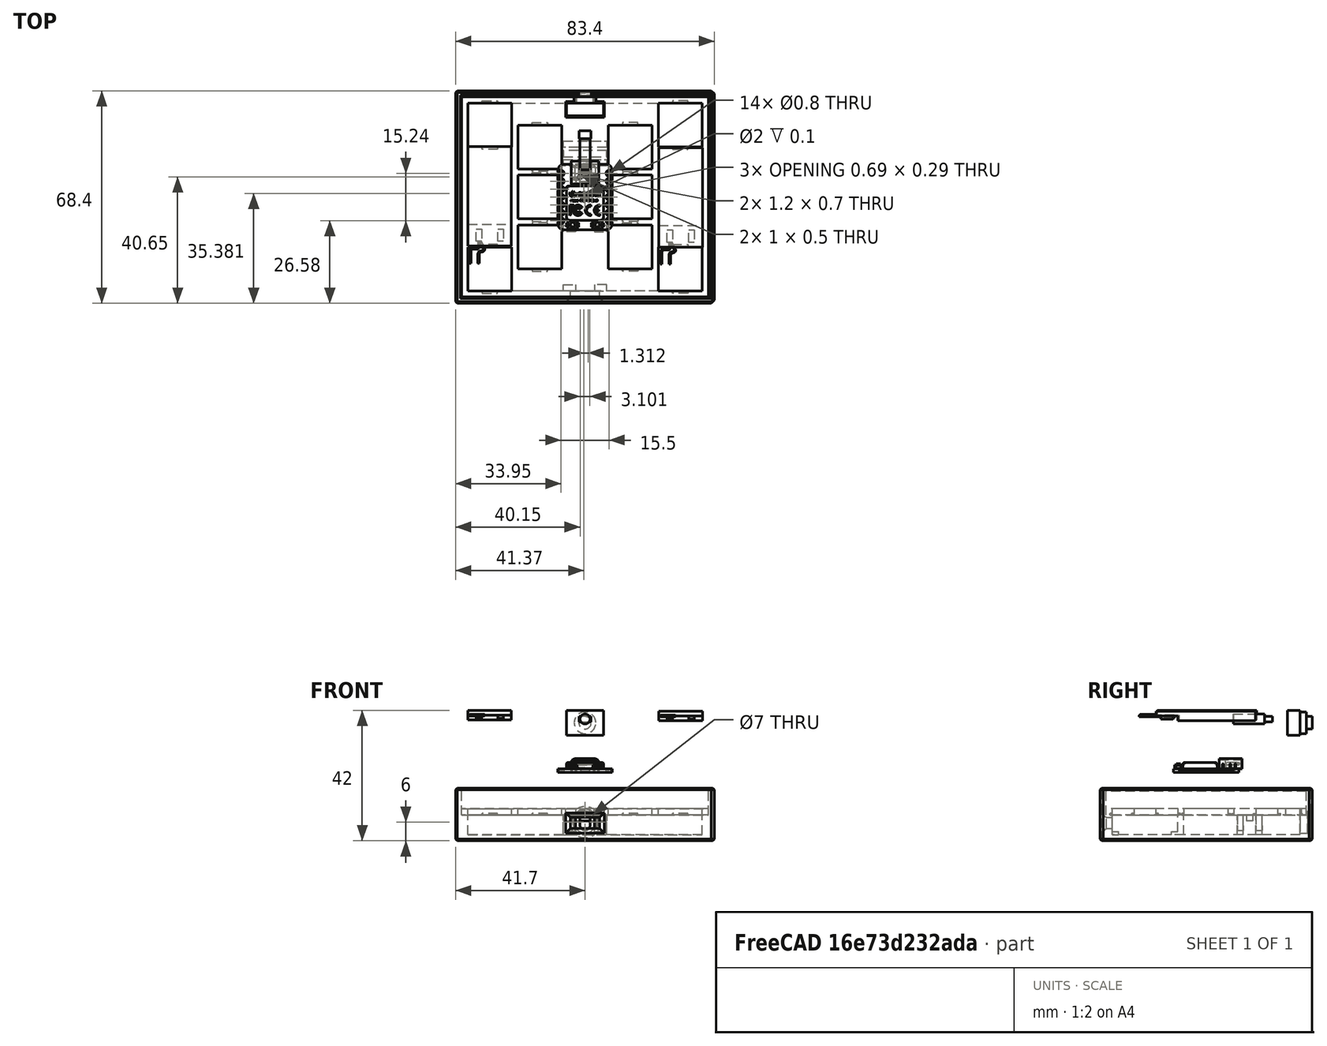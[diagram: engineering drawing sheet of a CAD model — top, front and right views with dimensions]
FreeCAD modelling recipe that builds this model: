
FCSTD DOCUMENT  (FreeCAD 0.20R)
Label: braille_keyboard
License: All rights reserved
LicenseURL: http://en.wikipedia.org/wiki/All_rights_reserved
objects: Sketcher::SketchObject×29, PartDesign::Pad×18, Mesh::Feature×10, Part::Feature×10, PartDesign::Body×6, App::Part×4, PartDesign::Plane×4, PartDesign::AdditivePipe×4, PartDesign::Pocket×3, Part::Chamfer×2, Spreadsheet::Sheet×1, Part::Box×1, Part::Cylinder×1, Part::MultiFuse×1, Part::Cut×1, PartDesign::Mirrored×1
note: 106 computed .brp shape members not serialized (recipe doc carries the construction recipe); baked Part::Feature solids carry a one-line shape summary decoded from their .brp

FEATURE [Spreadsheet::Sheet] Spreadsheet
  cells = A1=chamfer; B1=key size; C1=spacing; D1=walls; F1=xiauo width; G1=xiao length; H1=xiao height; I1=usb width; J1=usb height; A2(chamfer)==2mm; B2(keysize)==14.1mm; C2(spacing)==2mm; D2(walls)==2mm; F2(xiao_width)==18mm; G2(xiao_length)==21mm; I2(usb_width)==9.5mm; J2(usb_height)==3.5mm; C3=outer space; A4=mx height below; B4=mx height above; C4(outer_space)==2mm; F4=xiao add distance; A5(mx_height_below)==3.3mm + 5mm; B5(mx_height_above)==6.6mm; F5(xiao_add_dist)==-5mm; A8=pwr switch dia; B8=pwr switch height; A9(switch_dia)==7mm; B9(switch_height)==8mm; B13=Positioning of MX switches; B15=col1; C15=col2; D15=col3; E15=col4; B16(col1)==col2 - (keysize + spacing); C16(col2)==-((xiao_width + xiao_add_dist) / 2 + (keysize + spacing) / 2); D16(col3)==(xiao_width + xiao_add_dist) / 2 + (keysize + spacing) / 2; E16(col4)==col3 + keysize + spacing; B18=row1; C18=row2; D18=row3; E18=row4; B19(row1)==row2 + keysize + spacing; C19(row2)==0mm; D19(row3)==-(row2 + keysize + spacing); E19(row4)==row3 - keysize / 2; B22=snaplength; C22=snapwidth; B23(snaplength)==spacing / 2 - spacing / 10; C23(snapwidth)==5mm
FEATURE [Sketcher::SketchObject] Sketch001
  AttachmentOffset = pos=(0,0,20) rot=(0,0,1;0rad)
  FullyConstrained = true
  MapMode = 5
  Placement = pos=(0,0,20) rot=(0,0,1;0rad)
  Support = -> [XY_Plane001]
  expr: Constraints[8] = <<Spreadsheet>>.keysize * 4 + <<Spreadsheet>>.spacing * 2 + <<Spreadsheet>>.outer_space * 2 + <<Spreadsheet>>.walls * 2
  expr: Constraints[9] = <<Spreadsheet>>.keysize * 4 + <<Spreadsheet>>.spacing * 3 + <<Spreadsheet>>.outer_space * 2 + <<Spreadsheet>>.walls * 2 + <<Spreadsheet>>.xiao_width + <<Spreadsheet>>.xiao_add_dist
  sketch-geometry (8):
    g0: LineSegment StartX=-41.7 StartY=34.2 StartZ=0 EndX=41.7 EndY=34.2 EndZ=0
    g1: LineSegment StartX=41.7 StartY=34.2 StartZ=0 EndX=41.7 EndY=-34.2 EndZ=0
    g2: LineSegment StartX=41.7 StartY=-34.2 StartZ=0 EndX=-41.7 EndY=-34.2 EndZ=0
    g3: LineSegment StartX=-41.7 StartY=-34.2 StartZ=0 EndX=-41.7 EndY=34.2 EndZ=0
    g4: LineSegment StartX=-41.7 StartY=34.2 StartZ=0 EndX=41.7 EndY=34.2 EndZ=0
    g5: LineSegment StartX=41.7 StartY=34.2 StartZ=0 EndX=41.7 EndY=-34.2 EndZ=0
    g6: LineSegment StartX=41.7 StartY=-34.2 StartZ=0 EndX=-41.7 EndY=-34.2 EndZ=0
    g7: LineSegment StartX=-41.7 StartY=-34.2 StartZ=0 EndX=-41.7 EndY=34.2 EndZ=0
  constraints (20):
    c: Coincident(g0,g1)
    c: Coincident(g1,g2)
    c: Coincident(g2,g3)
    c: Coincident(g3,g0)
    c: Horizontal(g2)
    c: Vertical(g1)
    c: Symmetric(g0,g0,g-2)
    c: Symmetric(g2,g0,g-1)
    c: DistanceY(g3,g3) = 68.4
    c: DistanceX(g0,g0) = 83.4
    c: Coincident(g4,g5)
    c: Coincident(g5,g6)
    c: Coincident(g6,g7)
    c: Coincident(g7,g4)
    c: Horizontal(g4)
    c: Horizontal(g6)
    c: Vertical(g5)
    c: Vertical(g7)
    c: Coincident(g4,g0)
    c: Coincident(g5,g1)
FEATURE [PartDesign::Pad] Pad001  label="Bottom"
  Direction = (0,0,1)
  Length = 2
  Length2 = 10
  Profile = -> Sketch001
  ReferenceAxis = -> Sketch001 [N_Axis]
  Type = 0
  expr: Length = <<Spreadsheet>>.walls
FEATURE [Sketcher::SketchObject] Sketch002
  ExternalGeometry = -> [Pad001]
  FullyConstrained = true
  MapMode = 5
  Placement = pos=(0,0,20) rot=(1,0,0;3.14159rad)
  Support = -> [Pad001]
  expr: Constraints[16] = <<Spreadsheet>>.walls + <<Spreadsheet>>.outer_space
  expr: Constraints[19] = <<Spreadsheet>>.walls + <<Spreadsheet>>.outer_space
  sketch-geometry (8):
    g0: LineSegment StartX=-41.7 StartY=34.2 StartZ=0 EndX=41.7 EndY=34.2 EndZ=0
    g1: LineSegment StartX=41.7 StartY=34.2 StartZ=0 EndX=41.7 EndY=-34.2 EndZ=0
    g2: LineSegment StartX=41.7 StartY=-34.2 StartZ=0 EndX=-41.7 EndY=-34.2 EndZ=0
    g3: LineSegment StartX=-41.7 StartY=-34.2 StartZ=0 EndX=-41.7 EndY=34.2 EndZ=0
    g4: LineSegment StartX=-37.7 StartY=30.2 StartZ=0 EndX=37.7 EndY=30.2 EndZ=0
    g5: LineSegment StartX=37.7 StartY=30.2 StartZ=0 EndX=37.7 EndY=-30.2 EndZ=0
    g6: LineSegment StartX=37.7 StartY=-30.2 StartZ=0 EndX=-37.7 EndY=-30.2 EndZ=0
    g7: LineSegment StartX=-37.7 StartY=-30.2 StartZ=0 EndX=-37.7 EndY=30.2 EndZ=0
  constraints (20):
    c: Coincident(g0,g1)
    c: Coincident(g1,g2)
    c: Coincident(g2,g3)
    c: Coincident(g3,g0)
    c: Horizontal(g0)
    c: Horizontal(g2)
    c: Vertical(g1)
    c: Vertical(g3)
    c: Coincident(g0,g-4)
    c: Coincident(g1,g-6)
    c: Coincident(g4,g5)
    c: Coincident(g5,g6)
    c: Coincident(g6,g7)
    c: Coincident(g7,g4)
    c: Horizontal(g6)
    c: Vertical(g5)
    c: DistanceX(g0,g4) = 4
    c: Symmetric(g4,g4,g-2)
    c: Symmetric(g4,g6,g-1)
    c: DistanceY(g4,g0) = 4
FEATURE [PartDesign::Pad] Pad002  label="PlateRest"
  BaseFeature = -> Pad001
  Direction = (0,0,-1)
  Length = 6.3
  Length2 = 10
  Profile = -> Sketch002
  ReferenceAxis = -> Sketch002 [N_Axis]
  Type = 0
  expr: Length = <<Spreadsheet>>.mx_height_below - <<Spreadsheet>>.walls
FEATURE [Sketcher::SketchObject] Sketch003
  ExternalGeometry = -> [Pad002]
  FullyConstrained = true
  MapMode = 5
  Placement = pos=(0,0,13.7) rot=(1,0,0;3.14159rad)
  Support = -> [Pad002]
  expr: Constraints[8] = <<Spreadsheet>>.walls
  expr: Constraints[9] = <<Spreadsheet>>.walls
  sketch-geometry (8):
    g0: LineSegment StartX=-39.7 StartY=32.2 StartZ=0 EndX=39.7 EndY=32.2 EndZ=0
    g1: LineSegment StartX=39.7 StartY=32.2 StartZ=0 EndX=39.7 EndY=-32.2 EndZ=0
    g2: LineSegment StartX=39.7 StartY=-32.2 StartZ=0 EndX=-39.7 EndY=-32.2 EndZ=0
    g3: LineSegment StartX=-39.7 StartY=-32.2 StartZ=0 EndX=-39.7 EndY=32.2 EndZ=0
    g4: LineSegment StartX=-41.7 StartY=34.2 StartZ=0 EndX=41.7 EndY=34.2 EndZ=0
    g5: LineSegment StartX=41.7 StartY=34.2 StartZ=0 EndX=41.7 EndY=-34.2 EndZ=0
    g6: LineSegment StartX=41.7 StartY=-34.2 StartZ=0 EndX=-41.7 EndY=-34.2 EndZ=0
    g7: LineSegment StartX=-41.7 StartY=-34.2 StartZ=0 EndX=-41.7 EndY=34.2 EndZ=0
  constraints (20):
    c: Coincident(g0,g1)
    c: Coincident(g1,g2)
    c: Coincident(g2,g3)
    c: Coincident(g3,g0)
    c: Horizontal(g2)
    c: Vertical(g1)
    c: Symmetric(g0,g0,g-2)
    c: Symmetric(g2,g0,g-1)
    c: DistanceY(g0,g-5) = 2
    c: DistanceX(g-5,g0) = 2
    c: Coincident(g4,g5)
    c: Coincident(g5,g6)
    c: Coincident(g6,g7)
    c: Coincident(g7,g4)
    c: Horizontal(g4)
    c: Horizontal(g6)
    c: Vertical(g5)
    c: Vertical(g7)
    c: Coincident(g4,g-5)
    c: Coincident(g5,g-6)
FEATURE [PartDesign::Pad] Pad003  label="OuterWall"
  BaseFeature = -> Pad002
  Direction = (0,0,-1)
  Length = 8.6
  Length2 = 10
  Profile = -> Sketch003
  ReferenceAxis = -> Sketch003 [N_Axis]
  Type = 0
  expr: Length = <<Spreadsheet>>.mx_height_above + <<Spreadsheet>>.walls
FEATURE [Mesh::Feature] switch_mx
  Placement = pos=(14.55,16.1,-1.4) rot=(1,0,0;3.14159rad)
  expr: .Placement.Base.x = <<Spreadsheet>>.col3
  expr: .Placement.Base.y = <<Spreadsheet>>.row1
FEATURE [Mesh::Feature] switch_mx001
  Placement = pos=(-14.55,0,-1.4) rot=(1,0,0;3.14159rad)
  expr: .Placement.Base.x = <<Spreadsheet>>.col2
  expr: .Placement.Base.y = <<Spreadsheet>>.row2
FEATURE [Sketcher::SketchObject] Sketch004
  ExternalGeometry = -> [Pad003]
  FullyConstrained = true
  MapMode = 5
  Placement = pos=(0,0,20) rot=(1,0,0;3.14159rad)
  Support = -> [Pad003]
  expr: Constraints[13] = <<Spreadsheet>>.walls
  expr: Constraints[28] = <<Spreadsheet>>.walls
  expr: Constraints[39] = <<Spreadsheet>>.walls
  expr: Constraints[40] = <<Spreadsheet>>.walls * 2
  expr: Constraints[60] = <<Spreadsheet>>.walls
  expr: Constraints[63] = 2 * <<Spreadsheet>>.walls
  expr: Constraints[7] = <<Spreadsheet>>.xiao_width
  expr: Constraints[8] = <<Spreadsheet>>.xiao_length
  sketch-geometry (22):
    g0: LineSegment StartX=-9 StartY=30.2 StartZ=0 EndX=9 EndY=30.2 EndZ=0
    g1: LineSegment StartX=9 StartY=30.2 StartZ=0 EndX=9 EndY=9.2 EndZ=0
    g2: LineSegment StartX=9 StartY=9.2 StartZ=0 EndX=-9 EndY=9.2 EndZ=0
    g3: LineSegment StartX=-9 StartY=9.2 StartZ=0 EndX=-9 EndY=30.2 EndZ=0
    g4: LineSegment StartX=-7 StartY=9.2 StartZ=0 EndX=-7 EndY=-30.2 EndZ=0
    g5: LineSegment StartX=7 StartY=9.2 StartZ=0 EndX=7 EndY=-30.2 EndZ=0
    g6: LineSegment StartX=-7 StartY=-10 StartZ=0 EndX=7 EndY=-10 EndZ=0
    g7: LineSegment StartX=7 StartY=-10 StartZ=0 EndX=7 EndY=-12 EndZ=0
    g8: LineSegment StartX=7 StartY=-12 StartZ=0 EndX=-7 EndY=-12 EndZ=0
    g9: LineSegment StartX=-7 StartY=-12 StartZ=0 EndX=-7 EndY=-10 EndZ=0
    g10: LineSegment StartX=-7 StartY=-16 StartZ=0 EndX=7 EndY=-16 EndZ=0
    g11: LineSegment StartX=7 StartY=-16 StartZ=0 EndX=7 EndY=-18 EndZ=0
    g12: LineSegment StartX=7 StartY=-18 StartZ=0 EndX=-7 EndY=-18 EndZ=0
    g13: LineSegment StartX=-7 StartY=-18 StartZ=0 EndX=-7 EndY=-16 EndZ=0
    g14: LineSegment StartX=-7 StartY=9.2 StartZ=0 EndX=-3 EndY=9.2 EndZ=0
    g15: LineSegment StartX=-3 StartY=9.2 StartZ=0 EndX=-3 EndY=7.2 EndZ=0
    g16: LineSegment StartX=-3 StartY=7.2 StartZ=0 EndX=-7 EndY=7.2 EndZ=0
    g17: LineSegment StartX=-7 StartY=7.2 StartZ=0 EndX=-7 EndY=9.2 EndZ=0
    g18: LineSegment StartX=3 StartY=9.2 StartZ=0 EndX=7 EndY=9.2 EndZ=0
    g19: LineSegment StartX=7 StartY=9.2 StartZ=0 EndX=7 EndY=7.2 EndZ=0
    g20: LineSegment StartX=7 StartY=7.2 StartZ=0 EndX=3 EndY=7.2 EndZ=0
    g21: LineSegment StartX=3 StartY=7.2 StartZ=0 EndX=3 EndY=9.2 EndZ=0
  constraints (64):
    c: Coincident(g0,g1)
    c: Coincident(g1,g2)
    c: Coincident(g2,g3)
    c: Coincident(g3,g0)
    c: Horizontal(g2)
    c: Vertical(g1)
    c: Vertical(g3)
    c: DistanceX(g0,g0) = 18
    c: DistanceY(g1,g1) = 21
    c: Symmetric(g0,g0,g-2)
    c: PointOnObject(g0,g-3)
    c: PointOnObject(g4,g2)
    c: Symmetric(g4,g5,g-2)
    c: DistanceX(g2,g4) = 2
    c: PointOnObject(g4,g-6)
    c: Vertical(g4)
    c: PointOnObject(g5,g-6)
    c: Vertical(g5)
    c: Coincident(g6,g7)
    c: Coincident(g7,g8)
    c: Coincident(g8,g9)
    c: Coincident(g9,g6)
    c: Horizontal(g6)
    c: Horizontal(g8)
    c: Vertical(g7)
    c: Vertical(g9)
    c: PointOnObject(g6,g4)
    c: PointOnObject(g7,g5)
    c: DistanceY(g7,g7) = 2
    c: Coincident(g10,g11)
    c: Coincident(g11,g12)
    c: Coincident(g12,g13)
    c: Coincident(g13,g10)
    c: Horizontal(g10)
    c: Horizontal(g12)
    c: Vertical(g11)
    c: Vertical(g13)
    c: PointOnObject(g10,g4)
    c: PointOnObject(g11,g5)
    c: DistanceY(g11,g11) = 2
    c: DistanceY(g10,g7) = 4
    c: DistanceY(g6,g-1) = 10
    c: Coincident(g14,g15)
    c: Coincident(g15,g16)
    c: Coincident(g16,g17)
    c: Coincident(g17,g14)
    c: Horizontal(g14)
    c: Horizontal(g16)
    c: Vertical(g15)
    c: Vertical(g17)
    c: Coincident(g14,g4)
    c: Coincident(g18,g19)
    c: Coincident(g19,g20)
    c: Coincident(g20,g21)
    c: Coincident(g21,g18)
    c: Horizontal(g18)
    c: Horizontal(g20)
    c: Vertical(g19)
    c: Vertical(g21)
    c: PointOnObject(g19,g5)
    c: DistanceY(g15,g15) = 2
    c: Equal(g15,g21)
    c: Symmetric(g18,g14,g-2)
    c: DistanceX(g20,g20) = 4
FEATURE [PartDesign::Pad] Pad004  label="xiaoholder"
  BaseFeature = -> Pad003
  Direction = (0,0,-1)
  Length = 6.3
  Length2 = 10
  Profile = -> Sketch004
  ReferenceAxis = -> Sketch004 [N_Axis]
  Type = 0
  expr: Length = <<Spreadsheet>>.mx_height_below - <<Spreadsheet>>.walls
FEATURE [Sketcher::SketchObject] Sketch005
  ExternalGeometry = -> [Pad004]
  FullyConstrained = true
  MapMode = 5
  Placement = pos=(0,0,20) rot=(1,0,0;3.14159rad)
  Support = -> [Pad004]
  expr: Constraints[25] = <<Spreadsheet>>.walls
  expr: Constraints[9] = <<Spreadsheet>>.walls
  sketch-geometry (20):
    g0: LineSegment StartX=-7 StartY=9.2 StartZ=0 EndX=-3 EndY=9.2 EndZ=0
    g1: LineSegment StartX=-3 StartY=9.2 StartZ=0 EndX=-3 EndY=11.2 EndZ=0
    g2: LineSegment StartX=-3 StartY=11.2 StartZ=0 EndX=-7 EndY=11.2 EndZ=0
    g3: LineSegment StartX=-7 StartY=11.2 StartZ=0 EndX=-7 EndY=9.2 EndZ=0
    g4: LineSegment StartX=-3 StartY=30.2 StartZ=0 EndX=-7 EndY=30.2 EndZ=0
    g5: LineSegment StartX=-7 StartY=30.2 StartZ=0 EndX=-7 EndY=28.2 EndZ=0
    g6: LineSegment StartX=-7 StartY=28.2 StartZ=0 EndX=-3 EndY=28.2 EndZ=0
    g7: LineSegment StartX=-3 StartY=28.2 StartZ=0 EndX=-3 EndY=30.2 EndZ=0
    g8: LineSegment StartX=-3 StartY=11.2 StartZ=0 EndX=-3 EndY=30.2 EndZ=0
    g9: LineSegment StartX=-7 StartY=11.2 StartZ=0 EndX=-7 EndY=30.2 EndZ=0
    g10: LineSegment StartX=7 StartY=9.2 StartZ=0 EndX=3 EndY=9.2 EndZ=0
    g11: LineSegment StartX=3 StartY=9.2 StartZ=0 EndX=3 EndY=11.2 EndZ=0
    g12: LineSegment StartX=3 StartY=11.2 StartZ=0 EndX=7 EndY=11.2 EndZ=0
    g13: LineSegment StartX=7 StartY=11.2 StartZ=0 EndX=7 EndY=9.2 EndZ=0
    g14: LineSegment StartX=3 StartY=30.2 StartZ=0 EndX=7 EndY=30.2 EndZ=0
    g15: LineSegment StartX=7 StartY=30.2 StartZ=0 EndX=7 EndY=28.2 EndZ=0
    g16: LineSegment StartX=7 StartY=28.2 StartZ=0 EndX=3 EndY=28.2 EndZ=0
    g17: LineSegment StartX=3 StartY=28.2 StartZ=0 EndX=3 EndY=30.2 EndZ=0
    g18: LineSegment StartX=3 StartY=11.2 StartZ=0 EndX=3 EndY=30.2 EndZ=0
    g19: LineSegment StartX=7 StartY=11.2 StartZ=0 EndX=7 EndY=30.2 EndZ=0
  constraints (52):
    c: Coincident(g0,g1)
    c: Coincident(g1,g2)
    c: Coincident(g2,g3)
    c: Coincident(g3,g0)
    c: Horizontal(g2)
    c: Vertical(g1)
    c: Vertical(g3)
    c: Coincident(g0,g-3)
    c: Coincident(g0,g-3)
    c: DistanceY(g1,g1) = 2
    c: Coincident(g4,g5)
    c: Coincident(g5,g6)
    c: Coincident(g6,g7)
    c: Coincident(g7,g4)
    c: Horizontal(g4)
    c: Horizontal(g6)
    c: Vertical(g5)
    c: Vertical(g7)
    c: PointOnObject(g4,g-4)
    c: Coincident(g8,g1)
    c: Vertical(g8)
    c: Coincident(g9,g2)
    c: Vertical(g9)
    c: Coincident(g4,g9)
    c: Coincident(g4,g8)
    c: DistanceY(g5,g5) = 2
    c: Coincident(g10,g11)
    c: Coincident(g11,g12)
    c: Coincident(g12,g13)
    c: Coincident(g13,g10)
    c: Horizontal(g12)
    c: Vertical(g11)
    c: Vertical(g13)
    c: Coincident(g14,g15)
    c: Coincident(g15,g16)
    c: Coincident(g16,g17)
    c: Coincident(g17,g14)
    c: Horizontal(g14)
    c: Horizontal(g16)
    c: Vertical(g15)
    c: Vertical(g17)
    c: Coincident(g18,g11)
    c: Coincident(g19,g12)
    c: Vertical(g19)
    c: Coincident(g14,g19)
    c: Coincident(g14,g18)
    c: Symmetric(g14,g4,g-2)
    c: Equal(g17,g7)
    c: Symmetric(g11,g1,g-2)
    c: Equal(g11,g1)
    c: Horizontal(g10)
    c: Equal(g12,g2)
FEATURE [PartDesign::Pad] Pad005  label="xiaorest"
  BaseFeature = -> Pad004
  Direction = (0,0,-1)
  Length = 1
  Length2 = 10
  Profile = -> Sketch005
  ReferenceAxis = -> Sketch005 [N_Axis]
  Type = 0
FEATURE [Sketcher::SketchObject] Sketch006
  ExternalGeometry = -> [Pad005]
  FullyConstrained = true
  MapMode = 5
  Placement = pos=(0,-34.2,0) rot=(1,0,0;1.5708rad)
  Support = -> [Pad005]
  expr: Constraints[8] = <<Spreadsheet>>.usb_height
  expr: Constraints[9] = <<Spreadsheet>>.usb_width
  sketch-geometry (4):
    g0: LineSegment StartX=4.75 StartY=14.5 StartZ=0 EndX=-4.75 EndY=14.5 EndZ=0
    g1: LineSegment StartX=-4.75 StartY=14.5 StartZ=0 EndX=-4.75 EndY=18 EndZ=0
    g2: LineSegment StartX=-4.75 StartY=18 StartZ=0 EndX=4.75 EndY=18 EndZ=0
    g3: LineSegment StartX=4.75 StartY=18 StartZ=0 EndX=4.75 EndY=14.5 EndZ=0
  constraints (11):
    c: Coincident(g0,g1)
    c: Coincident(g1,g2)
    c: Coincident(g2,g3)
    c: Coincident(g3,g0)
    c: Horizontal(g2)
    c: Vertical(g1)
    c: Vertical(g3)
    c: Symmetric(g0,g0,g-2)
    c: DistanceY(g3,g3) = 3.5
    c: DistanceX(g0,g0) = 9.5
    c: DistanceY(g2,g-3) = 1
FEATURE [Part::Feature] Part__Feature  label="type-c v2"
  Placement = pos=(2.2e-14,4.2,2.8) rot=(0,1,0;3.14159rad)
  shape: bbox 8.954 x 7.914 x 4.214 mm, 384 faces, 24 solids (baked)
FEATURE [Part::Feature] Part__Feature001  label="smd_button v3"
  Placement = pos=(-4,-7.7,2.5) rot=(0,0,1;0rad)
  shape: bbox 4 x 2.5 x 1.6 mm, 76 faces (baked)
FEATURE [Part::Feature] Part__Feature002  label="Shell"
  shape: bbox 2.7 x 2.4 x 1.1 mm, 32 faces (baked)
FEATURE [Part::Feature] Part__Feature003  label="DOUT"
  shape: bbox 0.85 x 0.4 x 0.4 mm, 9 faces (baked)
FEATURE [Part::Feature] Part__Feature004  label="DIN"
  shape: bbox 0.85 x 0.4 x 0.4 mm, 9 faces (baked)
FEATURE [Part::Feature] Part__Feature005  label="VSS"
  shape: bbox 0.85 x 0.4 x 0.4 mm, 9 faces (baked)
FEATURE [Part::Feature] Part__Feature006  label="VDD"
  shape: bbox 0.85 x 0.4 x 0.4 mm, 9 faces (baked)
FEATURE [App::Part] SK6805_2_4x2_7_v1  label="SK6805-2.4x2.7 v1"
  Group = -> [Part__Feature002,Part__Feature003,Part__Feature004,Part__Feature005,Part__Feature006]
  Origin = -> Origin002
  Placement = pos=(0,-9,1.2) rot=(0,0,1;0rad)
FEATURE [Part::Feature] Part__Feature007  label="smd_button v3(Mirror)"
  Placement = pos=(4,-7.7,2.5) rot=(0,1,0;3.14159rad)
  shape: bbox 4 x 2.5 x 1.6 mm, 76 faces (baked)
FEATURE [Part::Feature] Part__Feature008  label="COMPOUND"
  shape: bbox 17.5 x 21 x 3.2 mm, 206 faces, 16 solids (baked)
FEATURE [App::Part] main
  Group = -> [Part__Feature,Part__Feature001,SK6805_2_4x2_7_v1,Part__Feature007,Part__Feature008]
  Origin = -> Origin003
FEATURE [Part::Feature] Part__Feature009  label="COMPOUND001"
  shape: bbox 10.02 x 7.868 x 0.01 mm, 427 faces, 36 solids (baked)
FEATURE [App::Part] Seeed_Studio_XIAO_RP2040_v26  label="Seeed Studio XIAO RP2040 v26"
  Group = -> [main,Part__Feature009]
  Origin = -> Origin004
  Placement = pos=(0,-19.7,19) rot=(1,0,0;3.14159rad)
  expr: .Placement.Base.y = -2 * (<<Spreadsheet>>.keysize + <<Spreadsheet>>.spacing) + <<Spreadsheet>>.xiao_length / 2 + <<Spreadsheet>>.outer_space / 2
FEATURE [PartDesign::Pocket] Pocket  label="UsbHole"
  BaseFeature = -> Pad005
  Direction = (0,1,-2e-16)
  Length = 5
  Length2 = 5
  Profile = -> Sketch006
  ReferenceAxis = -> Sketch006 [N_Axis]
  Type = 0
FEATURE [Sketcher::SketchObject] Sketch007
  ExternalGeometry = -> [Pocket]
  FullyConstrained = true
  MapMode = 5
  Placement = pos=(0,34.2,0) rot=(0,0.707107,0.707107;3.14159rad)
  Support = -> [Pocket]
  expr: Constraints[17] = <<Spreadsheet>>.switch_dia
  expr: Constraints[8] = <<Spreadsheet>>.switch_height
  sketch-geometry (8):
    g0: LineSegment StartX=6 StartY=20 StartZ=0 EndX=-6 EndY=20 EndZ=0
    g1: LineSegment StartX=-6 StartY=20 StartZ=0 EndX=-6 EndY=12 EndZ=0
    g2: LineSegment StartX=-6 StartY=12 StartZ=0 EndX=6 EndY=12 EndZ=0
    g3: LineSegment StartX=6 StartY=12 StartZ=0 EndX=6 EndY=20 EndZ=0
    g4: LineSegment StartX=6 StartY=12 StartZ=0 EndX=-6 EndY=20 EndZ=0
    g5: LineSegment StartX=6 StartY=20 StartZ=0 EndX=-6 EndY=12 EndZ=0
    g6: GeomPoint X=-1.6e-15 Y=16 Z=0
    g7: Circle CenterX=-1.6e-15 CenterY=16 CenterZ=0 NormalX=0 NormalY=0 NormalZ=1 AngleXU=0 Radius=3.5
  constraints (19):
    c: Coincident(g0,g1)
    c: Coincident(g1,g2)
    c: Coincident(g2,g3)
    c: Coincident(g3,g0)
    c: Horizontal(g0)
    c: Vertical(g1)
    c: Vertical(g3)
    c: Symmetric(g2,g1,g-2)
    c: DistanceY(g3,g3) = 8
    c: DistanceX(g2,g2) = 12
    c: Coincident(g4,g2)
    c: Coincident(g4,g0)
    c: Coincident(g5,g0)
    c: Coincident(g5,g1)
    c: PointOnObject(g6,g5)
    c: PointOnObject(g6,g4)
    c: Coincident(g7,g6)
    c: Diameter(g7) = 7
    c: DistanceY(g-1,g1) = 12
FEATURE [PartDesign::Pocket] Pocket001  label="switchHole"
  BaseFeature = -> Pocket
  Direction = (0,-1,2e-16)
  Length = 4
  Length2 = 5
  Profile = -> Sketch007
  ReferenceAxis = -> Sketch007 [N_Axis]
  Refine = true
  Type = 0
  expr: Length = 2 * <<Spreadsheet>>.walls
FEATURE [PartDesign::Body] Body001
  Group = -> [Sketch001,Pad001,Sketch002,Pad002,Sketch003,Pad003,Sketch004,Pad004,Sketch005,Pad005,Sketch006,Pocket,Sketch007,Pocket001]
  Origin = -> Origin001
  Tip = -> Pocket001
FEATURE [Sketcher::SketchObject] Sketch008
  FullyConstrained = true
  MapMode = 5
  Support = -> [XY_Plane005]
  sketch-geometry (4):
    g0: LineSegment StartX=-6 StartY=4 StartZ=0 EndX=6 EndY=4 EndZ=0
    g1: LineSegment StartX=6 StartY=4 StartZ=0 EndX=6 EndY=-4 EndZ=0
    g2: LineSegment StartX=6 StartY=-4 StartZ=0 EndX=-6 EndY=-4 EndZ=0
    g3: LineSegment StartX=-6 StartY=-4 StartZ=0 EndX=-6 EndY=4 EndZ=0
  constraints (10):
    c: Coincident(g0,g1)
    c: Coincident(g1,g2)
    c: Coincident(g2,g3)
    c: Coincident(g3,g0)
    c: Horizontal(g2)
    c: Vertical(g1)
    c: Symmetric(g0,g0,g-2)
    c: Symmetric(g0,g2,g-1)
    c: DistanceX(g0,g0) = 12
    c: DistanceY(g1,g1) = 8
FEATURE [PartDesign::Pad] Pad006
  Direction = (0,0,1)
  Length = 4
  Length2 = 10
  Profile = -> Sketch008
  ReferenceAxis = -> Sketch008 [N_Axis]
  Type = 0
FEATURE [Sketcher::SketchObject] Sketch009
  FullyConstrained = true
  MapMode = 5
  Placement = pos=(0,0,0) rot=(1,0,0;3.14159rad)
  Support = -> [Pad006]
  sketch-geometry (1):
    g0: Circle CenterX=0 CenterY=0 CenterZ=0 NormalX=0 NormalY=0 NormalZ=1 AngleXU=0 Radius=3.5
  constraints (2):
    c: Coincident(g0,g-1)
    c: Diameter(g0) = 7
FEATURE [PartDesign::Pad] Pad007
  BaseFeature = -> Pad006
  Direction = (0,0,-1)
  Length = 2
  Length2 = 10
  Profile = -> Sketch009
  ReferenceAxis = -> Sketch009 [N_Axis]
  Type = 0
FEATURE [Sketcher::SketchObject] Sketch010
  FullyConstrained = true
  MapMode = 5
  Placement = pos=(0,0,-2) rot=(1,0,0;3.14159rad)
  Support = -> [Pad007]
  sketch-geometry (1):
    g0: Circle CenterX=0 CenterY=0 CenterZ=0 NormalX=0 NormalY=0 NormalZ=1 AngleXU=0 Radius=2
  constraints (2):
    c: Coincident(g0,g-1)
    c: Diameter(g0) = 4
FEATURE [PartDesign::Pad] Pad008
  BaseFeature = -> Pad007
  Direction = (0,0,-1)
  Length = 2
  Length2 = 10
  Profile = -> Sketch010
  ReferenceAxis = -> Sketch010 [N_Axis]
  Type = 0
FEATURE [PartDesign::Body] Body002  label="power_switch"
  Group = -> [Sketch008,Pad006,Sketch009,Pad007,Sketch010,Pad008]
  Origin = -> Origin005
  Placement = pos=(0,30.2,16) rot=(1,0,0;1.5708rad)
  Tip = -> Pad008
  expr: .Placement.Base.y = 2 * (<<Spreadsheet>>.keysize + <<Spreadsheet>>.spacing) - <<Spreadsheet>>.walls / 2
FEATURE [Mesh::Feature] switch_mx002
  Placement = pos=(30.65,23.15,-1.4) rot=(1,0,0;3.14159rad)
  expr: .Placement.Base.x = <<Spreadsheet>>.col4
  expr: .Placement.Base.y = <<Spreadsheet>>.row1 + <<Spreadsheet>>.keysize / 2
FEATURE [Mesh::Feature] switch_mx003
  Placement = pos=(14.55,0,-1.4) rot=(1,0,0;3.14159rad)
  expr: .Placement.Base.x = <<Spreadsheet>>.col3
  expr: .Placement.Base.y = <<Spreadsheet>>.row2
FEATURE [Mesh::Feature] switch_mx004
  Placement = pos=(-30.65,23.15,-1.4) rot=(1,0,0;3.14159rad)
  expr: .Placement.Base.x = <<Spreadsheet>>.col1
  expr: .Placement.Base.y = <<Spreadsheet>>.row1 + <<Spreadsheet>>.keysize / 2
FEATURE [Mesh::Feature] switch_mx005
  Placement = pos=(-14.55,16.1,-1.4) rot=(1,0,0;3.14159rad)
  expr: .Placement.Base.x = <<Spreadsheet>>.col2
  expr: .Placement.Base.y = <<Spreadsheet>>.row1
FEATURE [Mesh::Feature] switch_mx006
  Placement = pos=(-14.55,-16.1,-1.4) rot=(1,0,0;3.14159rad)
  expr: .Placement.Base.x = <<Spreadsheet>>.col2
  expr: .Placement.Base.y = <<Spreadsheet>>.row3
FEATURE [Mesh::Feature] switch_mx007
  Placement = pos=(14.55,-16.1,-1.4) rot=(1,0,0;3.14159rad)
  expr: .Placement.Base.x = <<Spreadsheet>>.col3
  expr: .Placement.Base.y = <<Spreadsheet>>.row3
FEATURE [Mesh::Feature] switch_mx008
  Placement = pos=(-30.65,-23.15,-1.4) rot=(1,0,0;3.14159rad)
  expr: .Placement.Base.x = <<Spreadsheet>>.col1
  expr: .Placement.Base.y = <<Spreadsheet>>.row4
FEATURE [Mesh::Feature] switch_mx009
  Placement = pos=(30.65,-23.15,-1.4) rot=(1,0,0;3.14159rad)
  expr: .Placement.Base.x = <<Spreadsheet>>.col4
  expr: .Placement.Base.y = <<Spreadsheet>>.row4
FEATURE [Sketcher::SketchObject] Sketch011
  FullyConstrained = true
  MapMode = 5
  Placement = pos=(0,0,0) rot=(1,0,0;1.5708rad)
  Support = -> [XZ_Plane007]
  sketch-geometry (1):
    g0: Circle CenterX=0 CenterY=0 CenterZ=0 NormalX=0 NormalY=0 NormalZ=1 AngleXU=0 Radius=1.6
  constraints (2):
    c: Coincident(g0,g-1)
    c: Diameter(g0) = 3.2
FEATURE [PartDesign::Pad] Pad009
  Direction = (0,-1,-2e-16)
  Length = 10
  Length2 = 10
  Placement = pos=(0,0,0) rot=(1,0,0;1.5708rad)
  Profile = -> Sketch011
  ReferenceAxis = -> Sketch011 [N_Axis]
  Type = 0
FEATURE [Sketcher::SketchObject] Sketch012
  FullyConstrained = true
  MapMode = 5
  Placement = pos=(0,0,0) rot=(-1,0,0;1.5708rad)
  Support = -> [Pad009]
  sketch-geometry (4):
    g0: LineSegment StartX=-1.95 StartY=0.9 StartZ=0 EndX=1.95 EndY=0.9 EndZ=0
    g1: LineSegment StartX=1.95 StartY=0.9 StartZ=0 EndX=1.95 EndY=-0.9 EndZ=0
    g2: LineSegment StartX=1.95 StartY=-0.9 StartZ=0 EndX=-1.95 EndY=-0.9 EndZ=0
    g3: LineSegment StartX=-1.95 StartY=-0.9 StartZ=0 EndX=-1.95 EndY=0.9 EndZ=0
  constraints (10):
    c: Coincident(g0,g1)
    c: Coincident(g1,g2)
    c: Coincident(g2,g3)
    c: Coincident(g3,g0)
    c: Horizontal(g2)
    c: Vertical(g1)
    c: Symmetric(g0,g0,g-2)
    c: Symmetric(g2,g0,g-1)
    c: DistanceY(g3,g3) = 1.8
    c: DistanceX(g0,g0) = 3.9
FEATURE [PartDesign::Pad] Pad010
  BaseFeature = -> Pad009
  Direction = (0,1,2e-16)
  Length = 2.5
  Length2 = 10
  Placement = pos=(0,0,0) rot=(1,0,0;1.5708rad)
  Profile = -> Sketch012
  ReferenceAxis = -> Sketch012 [N_Axis]
  Type = 0
FEATURE [PartDesign::Body] Body003  label="rumbler"
  Group = -> [Sketch011,Pad009,Sketch012,Pad010]
  Origin = -> Origin007
  Placement = pos=(0,18.8,17.2) rot=(0,0,1;0rad)
  Tip = -> Pad010
FEATURE [Part::Box] Box  label="Cube"
  AttacherType = Attacher::AttachEngine3D
  Height = 10
  Length = 3.2
  Placement = pos=(-1.6,0,0) rot=(0,0,1;0rad)
  Width = 12.4
FEATURE [Part::Cylinder] Cylinder
  Angle = 360
  AttacherType = Attacher::AttachEngine3D
  FirstAngle = 0
  Height = 12.4
  Placement = pos=(0,12.4,10) rot=(1,0,0;1.5708rad)
  Radius = 1.6
  SecondAngle = 0
FEATURE [Part::MultiFuse] Fusion
  Placement = pos=(0,8.4,7.1) rot=(0,0,1;0rad)
  Shapes = -> [Box,Cylinder]
FEATURE [Part::Cut] Cut
  Base = -> Body001
  Tool = -> Fusion
FEATURE [Part::Chamfer] Chamfer
  Base = -> Cut
  Edges = 5 edges: [Edge10 r=1,Edge15 r1=1.5 r2=2.1,Edge16 r1=1.5 r2=2.1,Edge17 r1=1.5 r2=2.1,Edge18 r1=1.5 r2=2.1]
FEATURE [Part::Chamfer] Chamfer001  label="case"
  Base = -> Chamfer
  Edges = 19 edges: [Edge3 r=0.5,Edge4 r=0.5,Edge5 r=0.5,Edge6 r=0.5,Edge7 r=1,Edge12 r=0.5,Edge13 r=0.5,Edge14 r=0.5,Edge15 r=0.5,Edge16 r=0.5,Edge17 r=0.5,Edge18 r=0.5,Edge19 r=0.5,Edge20 r=0.5,Edge21 r=0.5,Edge22 r=0.5,Edge23 r=0.5,Edge24 r=1,Edge25 r=1]
  Placement = pos=(0,0,0) rot=(0,1,0;3.14159rad)
FEATURE [Sketcher::SketchObject] Sketch013
  FullyConstrained = true
  MapMode = 5
  Support = -> [XY_Plane008]
  sketch-geometry (4):
    g0: LineSegment StartX=-7 StartY=12.5 StartZ=0 EndX=7 EndY=12.5 EndZ=0
    g1: LineSegment StartX=7 StartY=12.5 StartZ=0 EndX=7 EndY=-12.5 EndZ=0
    g2: LineSegment StartX=7 StartY=-12.5 StartZ=0 EndX=-7 EndY=-12.5 EndZ=0
    g3: LineSegment StartX=-7 StartY=-12.5 StartZ=0 EndX=-7 EndY=12.5 EndZ=0
  constraints (10):
    c: Coincident(g0,g1)
    c: Coincident(g1,g2)
    c: Coincident(g2,g3)
    c: Coincident(g3,g0)
    c: Horizontal(g2)
    c: Vertical(g3)
    c: DistanceY(g1,g1) = 25
    c: DistanceX(g0,g0) = 14
    c: Symmetric(g0,g0,g-2)
    c: Symmetric(g0,g1,g-1)
FEATURE [PartDesign::Pad] Pad011
  Direction = (0,0,1)
  Length = 3
  Length2 = 10
  Profile = -> Sketch013
  ReferenceAxis = -> Sketch013 [N_Axis]
  Type = 0
FEATURE [Sketcher::SketchObject] Sketch014
  ExternalGeometry = -> [Pad011]
  FullyConstrained = true
  MapMode = 5
  Placement = pos=(0,0,0) rot=(1,0,0;3.14159rad)
  Support = -> [Pad011]
  sketch-geometry (4):
    g0: LineSegment StartX=-7 StartY=12.5 StartZ=0 EndX=7 EndY=12.5 EndZ=0
    g1: LineSegment StartX=7 StartY=12.5 StartZ=0 EndX=7 EndY=19.5 EndZ=0
    g2: LineSegment StartX=7 StartY=19.5 StartZ=0 EndX=-7 EndY=19.5 EndZ=0
    g3: LineSegment StartX=-7 StartY=19.5 StartZ=0 EndX=-7 EndY=12.5 EndZ=0
  constraints (10):
    c: Coincident(g0,g1)
    c: Coincident(g1,g2)
    c: Coincident(g2,g3)
    c: Coincident(g3,g0)
    c: Horizontal(g2)
    c: Vertical(g1)
    c: Vertical(g3)
    c: Coincident(g0,g-3)
    c: Coincident(g0,g-3)
    c: DistanceY(g1,g1) = 7
FEATURE [PartDesign::Pad] Pad012
  BaseFeature = -> Pad011
  Direction = (0,0,-1)
  Length = 1.5
  Length2 = 10
  Profile = -> Sketch014
  ReferenceAxis = -> Sketch014 [N_Axis]
  Reversed = true
  Type = 0
FEATURE [Sketcher::SketchObject] Sketch015
  ExternalGeometry = -> [Pad012]
  FullyConstrained = true
  MapMode = 5
  Placement = pos=(0,0,1.5) rot=(0,0,1;0rad)
  Support = -> [Pad012]
  sketch-geometry (17):
    g0: LineSegment StartX=-2.6 StartY=-14 StartZ=0 EndX=-4.4 EndY=-14 EndZ=0
    g1: LineSegment StartX=-4.4 StartY=-14 StartZ=0 EndX=-4.4 EndY=-18 EndZ=0
    g2: LineSegment StartX=-4.4 StartY=-18 StartZ=0 EndX=-2.6 EndY=-18 EndZ=0
    g3: LineSegment StartX=-2.6 StartY=-18 StartZ=0 EndX=-2.6 EndY=-14 EndZ=0
    g4: LineSegment StartX=-7 StartY=-12.5 StartZ=0 EndX=9e-16 EndY=-19.5 EndZ=0
    g5: LineSegment StartX=0 StartY=-12.5 StartZ=0 EndX=-7 EndY=-19.5 EndZ=0
    g6: GeomPoint X=-3.5 Y=-16 Z=0
    g7: LineSegment StartX=-2.6 StartY=-14 StartZ=0 EndX=-4.4 EndY=-18 EndZ=0
    g8: LineSegment StartX=-2.6 StartY=-18 StartZ=0 EndX=-4.4 EndY=-14 EndZ=0
    g9: GeomPoint X=-3.5 Y=-16 Z=0
    g10: LineSegment StartX=4.4 StartY=-14 StartZ=0 EndX=2.6 EndY=-14 EndZ=0
    g11: LineSegment StartX=2.6 StartY=-14 StartZ=0 EndX=2.6 EndY=-18 EndZ=0
    g12: LineSegment StartX=2.6 StartY=-18 StartZ=0 EndX=4.4 EndY=-18 EndZ=0
    g13: LineSegment StartX=4.4 StartY=-18 StartZ=0 EndX=4.4 EndY=-14 EndZ=0
    g14: LineSegment StartX=4.4 StartY=-14 StartZ=0 EndX=2.6 EndY=-18 EndZ=0
    g15: LineSegment StartX=4.4 StartY=-18 StartZ=0 EndX=2.6 EndY=-14 EndZ=0
    g16: GeomPoint X=3.5 Y=-16 Z=0
  constraints (42):
    c: Coincident(g0,g1)
    c: Coincident(g1,g2)
    c: Coincident(g2,g3)
    c: Coincident(g3,g0)
    c: Horizontal(g0)
    c: Horizontal(g2)
    c: Vertical(g1)
    c: Vertical(g3)
    c: Coincident(g4,g-3)
    c: PointOnObject(g4,g-4)
    c: PointOnObject(g4,g-2)
    c: PointOnObject(g5,g-3)
    c: Coincident(g5,g-4)
    c: PointOnObject(g5,g-2)
    c: PointOnObject(g6,g5)
    c: PointOnObject(g6,g4)
    c: Coincident(g7,g0)
    c: Coincident(g7,g1)
    c: Coincident(g8,g2)
    c: Coincident(g8,g0)
    c: PointOnObject(g9,g8)
    c: PointOnObject(g9,g7)
    c: Coincident(g10,g11)
    c: Coincident(g11,g12)
    c: Coincident(g12,g13)
    c: Coincident(g13,g10)
    c: Horizontal(g10)
    c: Horizontal(g12)
    c: Vertical(g11)
    c: Vertical(g13)
    c: Coincident(g14,g10)
    c: Coincident(g14,g11)
    c: Coincident(g15,g12)
    c: Coincident(g15,g10)
    c: PointOnObject(g16,g15)
    c: PointOnObject(g16,g14)
    c: Equal(g13,g1)
    c: Equal(g0,g10)
    c: Symmetric(g0,g10,g-2)
    c: DistanceX(g0,g0) = 1.8
    c: Coincident(g9,g6)
    c: DistanceY(g3,g3) = 4
FEATURE [PartDesign::Pad] Pad013
  BaseFeature = -> Pad012
  Direction = (0,0,1)
  Length = 1
  Length2 = 10
  Profile = -> Sketch015
  ReferenceAxis = -> Sketch015 [N_Axis]
  Type = 0
FEATURE [Sketcher::SketchObject] Sketch016
  ExternalGeometry = -> [Pad013]
  FullyConstrained = false
  MapMode = 5
  Placement = pos=(0,0,1.5) rot=(0,0,1;0rad)
  Support = -> [Pad013]
  sketch-geometry (5):
    g0: LineSegment StartX=3.6527 StartY=-18 StartZ=0 EndX=3.6527 EndY=-19.9557 EndZ=0
    g1: LineSegment StartX=3.90145 StartY=-20.2045 StartZ=0 EndX=5.253 EndY=-20.2045 EndZ=0
    g2: LineSegment StartX=6.27944 StartY=-21.2309 StartZ=0 EndX=6.27944 EndY=-25.0298 EndZ=0
    g3: ArcOfCircle CenterX=3.90145 CenterY=-19.9557 CenterZ=0 NormalX=0 NormalY=0 NormalZ=1 AngleXU=0 Radius=0.248751 StartAngle=3.14159 EndAngle=4.71239
    g4: ArcOfCircle CenterX=5.253 CenterY=-21.2309 CenterZ=0 NormalX=0 NormalY=0 NormalZ=1 AngleXU=0 Radius=1.02644 StartAngle=0 EndAngle=1.5708
  constraints (8):
    c: PointOnObject(g0,g-3)
    c: Vertical(g0)
    c: Horizontal(g1)
    c: Vertical(g2)
    c: Tangent(g0,g3) = -1.5708
    c: Tangent(g1,g3) = -1.5708
    c: Tangent(g1,g4) = 1.5708
    c: Tangent(g2,g4) = 1.5708
FEATURE [PartDesign::Plane] DatumPlane
  Length = 60
  MapMode = 6
  Placement = pos=(6.27944,-25.0298,1.5) rot=(1,0,0;1.5708rad)
  ResizeMode = 0
  Support = -> [Sketch016,Pad013]
  Width = 60
FEATURE [Sketcher::SketchObject] Sketch017
  FullyConstrained = true
  MapMode = 5
  Placement = pos=(6.27944,-25.0298,1.5) rot=(1,0,0;1.5708rad)
  Support = -> [DatumPlane]
  sketch-geometry (1):
    g0: Circle CenterX=0 CenterY=0 CenterZ=0 NormalX=0 NormalY=0 NormalZ=1 AngleXU=0 Radius=0.25
  constraints (2):
    c: Coincident(g0,g-1)
    c: Diameter(g0) = 0.5
FEATURE [PartDesign::AdditivePipe] AdditivePipe
  AuxilleryCurvelinear = true
  AuxillerySpineTangent = false
  BaseFeature = -> Pad013
  Binormal = (0,0,0)
  Mode = 0
  Profile = -> Sketch017
  Spine = -> Sketch016
  SpineTangent = false
  Transformation = 0
  Transition = 0
FEATURE [Sketcher::SketchObject] Sketch018
  ExternalGeometry = -> [AdditivePipe]
  FullyConstrained = false
  MapMode = 5
  Placement = pos=(0,0,1.5) rot=(0,0,1;0rad)
  Support = -> [AdditivePipe]
  sketch-geometry (5):
    g0: LineSegment StartX=3.07914 StartY=-18 StartZ=0 EndX=1.90544 EndY=-20.1586 EndZ=0
    g1: LineSegment StartX=2.28825 StartY=-21.0844 StartZ=0 EndX=2.98106 EndY=-21.2901 EndZ=0
    g2: LineSegment StartX=3.55483 StartY=-22.0589 StartZ=0 EndX=3.55483 EndY=-25.0439 EndZ=0
    g3: ArcOfCircle CenterX=2.47169 CenterY=-20.4665 CenterZ=0 NormalX=0 NormalY=0 NormalZ=1 AngleXU=0 Radius=0.64454 StartAngle=2.64358 EndAngle=4.4238
    g4: ArcOfCircle CenterX=2.75281 CenterY=-22.0589 CenterZ=0 NormalX=0 NormalY=0 NormalZ=1 AngleXU=0 Radius=0.802026 StartAngle=0 EndAngle=1.28221
  constraints (6):
    c: PointOnObject(g0,g-3)
    c: Vertical(g2)
    c: Tangent(g0,g3) = -1.5708
    c: Tangent(g1,g3) = -1.5708
    c: Tangent(g1,g4) = 1.5708
    c: Tangent(g2,g4) = 1.5708
FEATURE [PartDesign::Plane] DatumPlane001
  Length = 60
  MapMode = 6
  Placement = pos=(3.55483,-25.0439,1.5) rot=(1,0,0;1.5708rad)
  ResizeMode = 0
  Support = -> [Sketch018,AdditivePipe]
  Width = 60
FEATURE [Sketcher::SketchObject] Sketch019
  FullyConstrained = true
  MapMode = 5
  Placement = pos=(3.55483,-25.0439,1.5) rot=(1,0,0;1.5708rad)
  Support = -> [DatumPlane001]
  sketch-geometry (1):
    g0: Circle CenterX=0 CenterY=0 CenterZ=0 NormalX=0 NormalY=0 NormalZ=1 AngleXU=0 Radius=0.25
  constraints (2):
    c: Coincident(g0,g-1)
    c: Diameter(g0) = 0.5
FEATURE [PartDesign::AdditivePipe] AdditivePipe001
  AuxilleryCurvelinear = true
  AuxillerySpineTangent = false
  BaseFeature = -> AdditivePipe
  Binormal = (0,0,0)
  Mode = 0
  Profile = -> Sketch019
  Spine = -> Sketch018
  SpineTangent = false
  Transformation = 0
  Transition = 0
FEATURE [PartDesign::Body] Body004  label="Battery"
  Group = -> [Sketch013,Pad011,Sketch014,Pad012,Sketch015,Pad013,Sketch016,DatumPlane,Sketch017,AdditivePipe,Sketch018,DatumPlane001,Sketch019,AdditivePipe001]
  Origin = -> Origin008
  Placement = pos=(30.8,3.4,19.7) rot=(0,1,0;3.14159rad)
  Tip = -> AdditivePipe001
FEATURE [Sketcher::SketchObject] Sketch020
  FullyConstrained = true
  MapMode = 5
  Support = -> [XY_Plane009]
  expr: Constraints[114] = <<Spreadsheet>>.outer_space
  expr: Constraints[115] = <<Spreadsheet>>.outer_space
  expr: Constraints[116] = 1.5mm
  expr: Constraints[127] = <<Spreadsheet>>.spacing
  expr: Constraints[128] = <<Spreadsheet>>.keysize / 2
  expr: Constraints[15] = <<Spreadsheet>>.keysize
  expr: Constraints[16] = -<<Spreadsheet>>.col2
  expr: Constraints[17] = <<Spreadsheet>>.row1
  expr: Constraints[234] = <<Spreadsheet>>.outer_space
  expr: Constraints[235] = <<Spreadsheet>>.outer_space
  expr: Constraints[36] = <<Spreadsheet>>.keysize + <<Spreadsheet>>.spacing
  sketch-geometry (94):
    g0: LineSegment StartX=-21.6 StartY=23.15 StartZ=0 EndX=-7.5 EndY=23.15 EndZ=0
    g1: LineSegment StartX=-7.5 StartY=23.15 StartZ=0 EndX=-7.5 EndY=9.05 EndZ=0
    g2: LineSegment StartX=-7.5 StartY=9.05 StartZ=0 EndX=-21.6 EndY=9.05 EndZ=0
    g3: LineSegment StartX=-21.6 StartY=9.05 StartZ=0 EndX=-21.6 EndY=23.15 EndZ=0
    g4: LineSegment StartX=-21.6 StartY=23.15 StartZ=0 EndX=-7.5 EndY=9.05 EndZ=0
    g5: LineSegment StartX=-21.6 StartY=9.05 StartZ=0 EndX=-7.5 EndY=23.15 EndZ=0
    g6: GeomPoint X=-14.55 Y=16.1 Z=0
    g7: LineSegment StartX=-21.6 StartY=7.05 StartZ=0 EndX=-7.5 EndY=7.05 EndZ=0
    g8: LineSegment StartX=-7.5 StartY=7.05 StartZ=0 EndX=-7.5 EndY=-7.05 EndZ=0
    g9: LineSegment StartX=-7.5 StartY=-7.05 StartZ=0 EndX=-21.6 EndY=-7.05 EndZ=0
    g10: LineSegment StartX=-21.6 StartY=-7.05 StartZ=0 EndX=-21.6 EndY=7.05 EndZ=0
    g11: LineSegment StartX=-21.6 StartY=7.05 StartZ=0 EndX=-7.5 EndY=-7.05 EndZ=0
    g12: LineSegment StartX=-21.6 StartY=-7.05 StartZ=0 EndX=-7.5 EndY=7.05 EndZ=0
    g13: GeomPoint X=-14.55 Y=3e-16 Z=0
    g14: LineSegment StartX=-21.6 StartY=23.15 StartZ=0 EndX=-21.6 EndY=7.05 EndZ=0
    g15: LineSegment StartX=-21.6 StartY=-9.05 StartZ=0 EndX=-7.5 EndY=-9.05 EndZ=0
    g16: LineSegment StartX=-7.5 StartY=-9.05 StartZ=0 EndX=-7.5 EndY=-23.15 EndZ=0
    g17: LineSegment StartX=-7.5 StartY=-23.15 StartZ=0 EndX=-21.6 EndY=-23.15 EndZ=0
    g18: LineSegment StartX=-21.6 StartY=-23.15 StartZ=0 EndX=-21.6 EndY=-9.05 EndZ=0
    g19: LineSegment StartX=-21.6 StartY=-9.05 StartZ=0 EndX=-7.5 EndY=-23.15 EndZ=0
    g20: LineSegment StartX=-21.6 StartY=-23.15 StartZ=0 EndX=-7.5 EndY=-9.05 EndZ=0
    g21: GeomPoint X=-14.55 Y=-16.1 Z=0
    g22: LineSegment StartX=-21.6 StartY=7.05 StartZ=0 EndX=-21.6 EndY=-9.05 EndZ=0
    g23: LineSegment StartX=-37.7 StartY=-16.1 StartZ=0 EndX=-23.6 EndY=-16.1 EndZ=0
    g24: LineSegment StartX=-23.6 StartY=-16.1 StartZ=0 EndX=-23.6 EndY=-30.2 EndZ=0
    g25: LineSegment StartX=-23.6 StartY=-30.2 StartZ=0 EndX=-37.7 EndY=-30.2 EndZ=0
    g26: LineSegment StartX=-37.7 StartY=-30.2 StartZ=0 EndX=-37.7 EndY=-16.1 EndZ=0
    g27: LineSegment StartX=-37.7 StartY=-16.1 StartZ=0 EndX=-23.6 EndY=-30.2 EndZ=0
    g28: LineSegment StartX=-37.7 StartY=-30.2 StartZ=0 EndX=-23.6 EndY=-16.1 EndZ=0
    g29: GeomPoint X=-30.65 Y=-23.15 Z=0
    g30: LineSegment StartX=-37.7 StartY=30.2 StartZ=0 EndX=-23.6 EndY=30.2 EndZ=0
    g31: LineSegment StartX=-23.6 StartY=30.2 StartZ=0 EndX=-23.6 EndY=16.1 EndZ=0
    g32: LineSegment StartX=-23.6 StartY=16.1 StartZ=0 EndX=-37.7 EndY=16.1 EndZ=0
    g33: LineSegment StartX=-37.7 StartY=16.1 StartZ=0 EndX=-37.7 EndY=30.2 EndZ=0
    g34: LineSegment StartX=-37.7 StartY=30.2 StartZ=0 EndX=-23.6 EndY=16.1 EndZ=0
    g35: LineSegment StartX=-37.7 StartY=16.1 StartZ=0 EndX=-23.6 EndY=30.2 EndZ=0
    g36: GeomPoint X=-30.65 Y=23.15 Z=0
    g37: LineSegment StartX=39.7 StartY=32.2 StartZ=0 EndX=39.7 EndY=-32.2 EndZ=0
    g38: LineSegment StartX=39.7 StartY=-32.2 StartZ=0 EndX=-39.7 EndY=-32.2 EndZ=0
    g39: LineSegment StartX=-39.7 StartY=-32.2 StartZ=0 EndX=-39.7 EndY=32.2 EndZ=0
    g40: LineSegment StartX=-39.7 StartY=32.2 StartZ=0 EndX=-2.875 EndY=32.2 EndZ=0
    g41: LineSegment StartX=-2.875 StartY=32.2 StartZ=0 EndX=-2.875 EndY=30.7 EndZ=0
    g42: LineSegment StartX=-2.875 StartY=30.7 StartZ=0 EndX=-6.25 EndY=30.7 EndZ=0
    g43: LineSegment StartX=-6.25 StartY=30.7 StartZ=0 EndX=-6.25 EndY=25.7 EndZ=0
    g44: LineSegment StartX=-6.25 StartY=25.7 StartZ=0 EndX=6.25 EndY=25.7 EndZ=0
    g45: LineSegment StartX=6.25 StartY=25.7 StartZ=0 EndX=6.25 EndY=30.7 EndZ=0
    g46: LineSegment StartX=6.25 StartY=30.7 StartZ=0 EndX=2.875 EndY=30.7 EndZ=0
    g47: LineSegment StartX=2.875 StartY=30.7 StartZ=0 EndX=2.875 EndY=32.2 EndZ=0
    g48: LineSegment StartX=2.875 StartY=32.2 StartZ=0 EndX=39.7 EndY=32.2 EndZ=0
    g49: LineSegment StartX=-21.6 StartY=23.15 StartZ=0 EndX=-23.6 EndY=23.15 EndZ=0
    g50: LineSegment StartX=-23.6 StartY=30.2 StartZ=0 EndX=-23.6 EndY=23.15 EndZ=0
    g51: LineSegment StartX=-21.6 StartY=-23.15 StartZ=0 EndX=-23.6 EndY=-23.15 EndZ=0
    g52: LineSegment StartX=-23.6 StartY=-30.2 StartZ=0 EndX=-23.6 EndY=-23.15 EndZ=0
    g53: LineSegment StartX=21.6 StartY=23.15 StartZ=0 EndX=7.5 EndY=23.15 EndZ=0
    g54: LineSegment StartX=7.5 StartY=23.15 StartZ=0 EndX=7.5 EndY=9.05 EndZ=0
    g55: LineSegment StartX=7.5 StartY=9.05 StartZ=0 EndX=21.6 EndY=9.05 EndZ=0
    g56: LineSegment StartX=21.6 StartY=9.05 StartZ=0 EndX=21.6 EndY=23.15 EndZ=0
    g57: LineSegment StartX=21.6 StartY=23.15 StartZ=0 EndX=7.5 EndY=9.05 EndZ=0
    g58: LineSegment StartX=21.6 StartY=9.05 StartZ=0 EndX=7.5 EndY=23.15 EndZ=0
    g59: GeomPoint X=14.55 Y=16.1 Z=0
    g60: LineSegment StartX=21.6 StartY=7.05 StartZ=0 EndX=7.5 EndY=7.05 EndZ=0
    g61: LineSegment StartX=7.5 StartY=7.05 StartZ=0 EndX=7.5 EndY=-7.05 EndZ=0
    g62: LineSegment StartX=7.5 StartY=-7.05 StartZ=0 EndX=21.6 EndY=-7.05 EndZ=0
    g63: LineSegment StartX=21.6 StartY=-7.05 StartZ=0 EndX=21.6 EndY=7.05 EndZ=0
    g64: LineSegment StartX=21.6 StartY=7.05 StartZ=0 EndX=7.5 EndY=-7.05 EndZ=0
    g65: LineSegment StartX=21.6 StartY=-7.05 StartZ=0 EndX=7.5 EndY=7.05 EndZ=0
    g66: GeomPoint X=14.55 Y=0 Z=0
    g67: LineSegment StartX=21.6 StartY=23.15 StartZ=0 EndX=21.6 EndY=7.05 EndZ=0
    g68: LineSegment StartX=21.6 StartY=-9.05 StartZ=0 EndX=7.5 EndY=-9.05 EndZ=0
    g69: LineSegment StartX=7.5 StartY=-9.05 StartZ=0 EndX=7.5 EndY=-23.15 EndZ=0
    g70: LineSegment StartX=7.5 StartY=-23.15 StartZ=0 EndX=21.6 EndY=-23.15 EndZ=0
    g71: LineSegment StartX=21.6 StartY=-23.15 StartZ=0 EndX=21.6 EndY=-9.05 EndZ=0
    g72: LineSegment StartX=21.6 StartY=-9.05 StartZ=0 EndX=7.5 EndY=-23.15 EndZ=0
    g73: LineSegment StartX=21.6 StartY=-23.15 StartZ=0 EndX=7.5 EndY=-9.05 EndZ=0
    g74: GeomPoint X=14.55 Y=-16.1 Z=0
    g75: LineSegment StartX=21.6 StartY=7.05 StartZ=0 EndX=21.6 EndY=-9.05 EndZ=0
    g76: LineSegment StartX=37.7 StartY=-16.1 StartZ=0 EndX=23.6 EndY=-16.1 EndZ=0
    g77: LineSegment StartX=23.6 StartY=-16.1 StartZ=0 EndX=23.6 EndY=-30.2 EndZ=0
    g78: LineSegment StartX=23.6 StartY=-30.2 StartZ=0 EndX=37.7 EndY=-30.2 EndZ=0
    g79: LineSegment StartX=37.7 StartY=-30.2 StartZ=0 EndX=37.7 EndY=-16.1 EndZ=0
    g80: LineSegment StartX=37.7 StartY=-16.1 StartZ=0 EndX=23.6 EndY=-30.2 EndZ=0
    g81: LineSegment StartX=37.7 StartY=-30.2 StartZ=0 EndX=23.6 EndY=-16.1 EndZ=0
    g82: GeomPoint X=30.65 Y=-23.15 Z=0
    g83: LineSegment StartX=37.7 StartY=30.2 StartZ=0 EndX=23.6 EndY=30.2 EndZ=0
    g84: LineSegment StartX=23.6 StartY=30.2 StartZ=0 EndX=23.6 EndY=16.1 EndZ=0
    g85: LineSegment StartX=23.6 StartY=16.1 StartZ=0 EndX=37.7 EndY=16.1 EndZ=0
    g86: LineSegment StartX=37.7 StartY=16.1 StartZ=0 EndX=37.7 EndY=30.2 EndZ=0
    g87: LineSegment StartX=37.7 StartY=30.2 StartZ=0 EndX=23.6 EndY=16.1 EndZ=0
    g88: LineSegment StartX=37.7 StartY=16.1 StartZ=0 EndX=23.6 EndY=30.2 EndZ=0
    g89: GeomPoint X=30.65 Y=23.15 Z=0
    g90: LineSegment StartX=21.6 StartY=23.15 StartZ=0 EndX=23.6 EndY=23.15 EndZ=0
    g91: LineSegment StartX=23.6 StartY=30.2 StartZ=0 EndX=23.6 EndY=23.15 EndZ=0
    g92: LineSegment StartX=21.6 StartY=-23.15 StartZ=0 EndX=23.6 EndY=-23.15 EndZ=0
    g93: LineSegment StartX=23.6 StartY=-30.2 StartZ=0 EndX=23.6 EndY=-23.15 EndZ=0
  constraints (240):
    c: Coincident(g0,g1)
    c: Coincident(g1,g2)
    c: Coincident(g2,g3)
    c: Coincident(g3,g0)
    c: Horizontal(g0)
    c: Horizontal(g2)
    c: Vertical(g1)
    c: Vertical(g3)
    c: Coincident(g4,g0)
    c: Coincident(g4,g1)
    c: Coincident(g5,g2)
    c: Coincident(g5,g0)
    c: PointOnObject(g6,g4)
    c: PointOnObject(g6,g5)
    c: Equal(g0,g3)
    c: DistanceX(g0,g0) = 14.1
    c: DistanceX(g6,g-1) = 14.55
    c: DistanceY(g-1,g6) = 16.1
    c: Coincident(g7,g8)
    c: Coincident(g8,g9)
    c: Coincident(g9,g10)
    c: Coincident(g10,g7)
    c: Horizontal(g7)
    c: Horizontal(g9)
    c: Vertical(g8)
    c: Vertical(g10)
    c: Coincident(g11,g7)
    c: Coincident(g11,g8)
    c: Coincident(g12,g9)
    c: Coincident(g12,g7)
    c: PointOnObject(g13,g11)
    c: PointOnObject(g13,g12)
    c: Equal(g7,g10)
    c: Equal(g0,g7) = 14
    c: Coincident(g0,g14)
    c: Coincident(g7,g14)
    c: Distance(g14) = 16.1
    c: Angle(g14) = -1.5708
    c: Coincident(g15,g16)
    c: Coincident(g16,g17)
    c: Coincident(g17,g18)
    c: Coincident(g18,g15)
    c: Horizontal(g15)
    c: Horizontal(g17)
    c: Vertical(g16)
    c: Vertical(g18)
    c: Coincident(g19,g15)
    c: Coincident(g19,g16)
    c: Coincident(g20,g17)
    c: Coincident(g20,g15)
    c: PointOnObject(g21,g19)
    c: PointOnObject(g21,g20)
    c: Equal(g15,g18)
    c: Equal(g0,g15) = 14
    c: Coincident(g7,g22)
    c: Coincident(g15,g22)
    c: Equal(g14,g22)
    c: Parallel(g22,g14)
    c: Coincident(g23,g24)
    c: Coincident(g24,g25)
    c: Coincident(g25,g26)
    c: Coincident(g26,g23)
    c: Horizontal(g23)
    c: Horizontal(g25)
    c: Vertical(g24)
    c: Vertical(g26)
    c: Coincident(g27,g23)
    c: Coincident(g27,g24)
    c: Coincident(g28,g25)
    c: Coincident(g28,g23)
    c: PointOnObject(g29,g27)
    c: PointOnObject(g29,g28)
    c: Equal(g23,g26)
    c: Equal(g0,g23) = 14
    c: Coincident(g30,g31)
    c: Coincident(g31,g32)
    c: Coincident(g32,g33)
    c: Coincident(g33,g30)
    c: Horizontal(g30)
    c: Horizontal(g32)
    c: Vertical(g31)
    c: Vertical(g33)
    c: Coincident(g34,g30)
    c: Coincident(g34,g31)
    c: Coincident(g35,g32)
    c: Coincident(g35,g30)
    c: PointOnObject(g36,g34)
    c: PointOnObject(g36,g35)
    c: Equal(g30,g33)
    c: Equal(g0,g30) = 14
    c: Coincident(g37,g38)
    c: Coincident(g38,g39)
    c: Vertical(g37)
    c: Coincident(g39,g40)
    c: Horizontal(g40)
    c: Coincident(g40,g41)
    c: Coincident(g41,g42)
    c: Coincident(g42,g43)
    c: Coincident(g43,g44)
    c: Horizontal(g44)
    c: Coincident(g44,g45)
    c: Vertical(g45)
    c: Coincident(g45,g46)
    c: Horizontal(g46)
    c: Coincident(g46,g47)
    c: Coincident(g47,g48)
    c: Coincident(g48,g37)
    c: Horizontal(g48)
    c: Vertical(g41)
    c: Vertical(g43)
    c: Horizontal(g42)
    c: Vertical(g47)
    c: Symmetric(g42,g45,g-2)
    c: Symmetric(g40,g47,g-2)
    c: DistanceY(g30,g39) = 2
    c: DistanceX(g39,g30) = 2
    c: DistanceY(g41,g41) = 1.5
    c: DistanceX(g44,g44) = 12.5
    c: DistanceY(g45,g45) = 5
    c: DistanceX(g40,g47) = 5.75
    c: Symmetric(g39,g38,g-1)
    c: Symmetric(g37,g38,g-2)
    c: Coincident(g49,g0)
    c: PointOnObject(g49,g31)
    c: Horizontal(g49)
    c: Coincident(g50,g30)
    c: Coincident(g50,g49)
    c: DistanceX(g49,g49) = 2
    c: DistanceY(g50,g50) = 7.05
    c: Coincident(g51,g17)
    c: PointOnObject(g51,g24)
    c: Horizontal(g51)
    c: Coincident(g52,g24)
    c: Coincident(g52,g51)
    c: Equal(g51,g49)
    c: Equal(g50,g52)
    c: Coincident(g53,g54)
    c: Coincident(g54,g55)
    c: Coincident(g55,g56)
    c: Coincident(g56,g53)
    c: Horizontal(g53)
    c: Horizontal(g55)
    c: Vertical(g54)
    c: Vertical(g56)
    c: Coincident(g57,g53)
    c: Coincident(g57,g54)
    c: Coincident(g58,g55)
    c: Coincident(g58,g53)
    c: PointOnObject(g59,g57)
    c: PointOnObject(g59,g58)
    c: Equal(g53,g56)
    c: Coincident(g60,g61)
    c: Coincident(g61,g62)
    c: Coincident(g62,g63)
    c: Coincident(g63,g60)
    c: Horizontal(g60)
    c: Horizontal(g62)
    c: Vertical(g61)
    c: Vertical(g63)
    c: Coincident(g64,g60)
    c: Coincident(g64,g61)
    c: Coincident(g65,g62)
    c: Coincident(g65,g60)
    c: PointOnObject(g66,g64)
    c: PointOnObject(g66,g65)
    c: Equal(g60,g63)
    c: Equal(g53,g60) = 14
    c: Coincident(g53,g67)
    c: Coincident(g60,g67)
    c: Angle(g67) = -1.5708
    c: Coincident(g68,g69)
    c: Coincident(g69,g70)
    c: Coincident(g70,g71)
    c: Coincident(g71,g68)
    c: Horizontal(g68)
    c: Horizontal(g70)
    c: Vertical(g69)
    c: Vertical(g71)
    c: Coincident(g72,g68)
    c: Coincident(g72,g69)
    c: Coincident(g73,g70)
    c: Coincident(g73,g68)
    c: PointOnObject(g74,g72)
    c: PointOnObject(g74,g73)
    c: Equal(g68,g71)
    c: Equal(g53,g68) = 14
    c: Coincident(g60,g75)
    c: Coincident(g68,g75)
    c: Equal(g67,g75)
    c: Parallel(g75,g67)
    c: Coincident(g76,g77)
    c: Coincident(g77,g78)
    c: Coincident(g78,g79)
    c: Coincident(g79,g76)
    c: Horizontal(g76)
    c: Horizontal(g78)
    c: Vertical(g77)
    c: Vertical(g79)
    c: Coincident(g80,g76)
    c: Coincident(g80,g77)
    c: Coincident(g81,g78)
    c: Coincident(g81,g76)
    c: PointOnObject(g82,g80)
    c: PointOnObject(g82,g81)
    c: Equal(g76,g79)
    c: Equal(g53,g76) = 14
    c: Coincident(g83,g84)
    c: Coincident(g84,g85)
    c: Coincident(g85,g86)
    c: Coincident(g86,g83)
    c: Horizontal(g83)
    c: Horizontal(g85)
    c: Vertical(g84)
    c: Vertical(g86)
    c: Coincident(g87,g83)
    c: Coincident(g87,g84)
    c: Coincident(g88,g85)
    c: Coincident(g88,g83)
    c: PointOnObject(g89,g87)
    c: PointOnObject(g89,g88)
    c: Equal(g83,g86)
    c: Equal(g53,g83) = 14
    c: Coincident(g90,g53)
    c: PointOnObject(g90,g84)
    c: Horizontal(g90)
    c: Coincident(g91,g83)
    c: Coincident(g91,g90)
    c: Coincident(g92,g70)
    c: PointOnObject(g92,g77)
    c: Horizontal(g92)
    c: Coincident(g93,g77)
    c: Coincident(g93,g92)
    c: Equal(g92,g90)
    c: Equal(g91,g93)
    c: DistanceY(g83,g37) = 2
    c: DistanceX(g83,g37) = 2
    c: Equal(g83,g30)
    c: Equal(g90,g49)
    c: Equal(g50,g91)
    c: PointOnObject(g66,g-1)
FEATURE [PartDesign::Pad] Pad014
  Direction = (0,0,1)
  Length = 2
  Length2 = 10
  Profile = -> Sketch020
  ReferenceAxis = -> Sketch020 [N_Axis]
  Type = 0
  expr: Length = <<Spreadsheet>>.walls
FEATURE [Sketcher::SketchObject] Sketch021
  FullyConstrained = true
  MapMode = 5
  Support = -> [XY_Plane010]
  sketch-geometry (4):
    g0: LineSegment StartX=-7 StartY=12.5 StartZ=0 EndX=7 EndY=12.5 EndZ=0
    g1: LineSegment StartX=7 StartY=12.5 StartZ=0 EndX=7 EndY=-12.5 EndZ=0
    g2: LineSegment StartX=7 StartY=-12.5 StartZ=0 EndX=-7 EndY=-12.5 EndZ=0
    g3: LineSegment StartX=-7 StartY=-12.5 StartZ=0 EndX=-7 EndY=12.5 EndZ=0
  constraints (10):
    c: Coincident(g0,g1)
    c: Coincident(g1,g2)
    c: Coincident(g2,g3)
    c: Coincident(g3,g0)
    c: Horizontal(g2)
    c: Vertical(g3)
    c: DistanceY(g1,g1) = 25
    c: DistanceX(g0,g0) = 14
    c: Symmetric(g0,g0,g-2)
    c: Symmetric(g0,g1,g-1)
FEATURE [PartDesign::Pad] Pad015
  Direction = (0,0,1)
  Length = 3
  Length2 = 10
  Profile = -> Sketch021
  ReferenceAxis = -> Sketch021 [N_Axis]
  Type = 0
FEATURE [Sketcher::SketchObject] Sketch022
  ExternalGeometry = -> [Pad015]
  FullyConstrained = true
  MapMode = 5
  Placement = pos=(0,0,0) rot=(1,0,0;3.14159rad)
  Support = -> [Pad015]
  sketch-geometry (4):
    g0: LineSegment StartX=-7 StartY=12.5 StartZ=0 EndX=7 EndY=12.5 EndZ=0
    g1: LineSegment StartX=7 StartY=12.5 StartZ=0 EndX=7 EndY=19.5 EndZ=0
    g2: LineSegment StartX=7 StartY=19.5 StartZ=0 EndX=-7 EndY=19.5 EndZ=0
    g3: LineSegment StartX=-7 StartY=19.5 StartZ=0 EndX=-7 EndY=12.5 EndZ=0
  constraints (10):
    c: Coincident(g0,g1)
    c: Coincident(g1,g2)
    c: Coincident(g2,g3)
    c: Coincident(g3,g0)
    c: Horizontal(g2)
    c: Vertical(g1)
    c: Vertical(g3)
    c: Coincident(g0,g-3)
    c: Coincident(g0,g-3)
    c: DistanceY(g1,g1) = 7
FEATURE [PartDesign::Pad] Pad016
  BaseFeature = -> Pad015
  Direction = (0,0,-1)
  Length = 1.5
  Length2 = 10
  Profile = -> Sketch022
  ReferenceAxis = -> Sketch022 [N_Axis]
  Reversed = true
  Type = 0
FEATURE [Sketcher::SketchObject] Sketch023
  ExternalGeometry = -> [Pad016]
  FullyConstrained = true
  MapMode = 5
  Placement = pos=(0,0,1.5) rot=(0,0,1;0rad)
  Support = -> [Pad016]
  sketch-geometry (17):
    g0: LineSegment StartX=-2.6 StartY=-14 StartZ=0 EndX=-4.4 EndY=-14 EndZ=0
    g1: LineSegment StartX=-4.4 StartY=-14 StartZ=0 EndX=-4.4 EndY=-18 EndZ=0
    g2: LineSegment StartX=-4.4 StartY=-18 StartZ=0 EndX=-2.6 EndY=-18 EndZ=0
    g3: LineSegment StartX=-2.6 StartY=-18 StartZ=0 EndX=-2.6 EndY=-14 EndZ=0
    g4: LineSegment StartX=-7 StartY=-12.5 StartZ=0 EndX=9e-16 EndY=-19.5 EndZ=0
    g5: LineSegment StartX=0 StartY=-12.5 StartZ=0 EndX=-7 EndY=-19.5 EndZ=0
    g6: GeomPoint X=-3.5 Y=-16 Z=0
    g7: LineSegment StartX=-2.6 StartY=-14 StartZ=0 EndX=-4.4 EndY=-18 EndZ=0
    g8: LineSegment StartX=-2.6 StartY=-18 StartZ=0 EndX=-4.4 EndY=-14 EndZ=0
    g9: GeomPoint X=-3.5 Y=-16 Z=0
    g10: LineSegment StartX=4.4 StartY=-14 StartZ=0 EndX=2.6 EndY=-14 EndZ=0
    g11: LineSegment StartX=2.6 StartY=-14 StartZ=0 EndX=2.6 EndY=-18 EndZ=0
    g12: LineSegment StartX=2.6 StartY=-18 StartZ=0 EndX=4.4 EndY=-18 EndZ=0
    g13: LineSegment StartX=4.4 StartY=-18 StartZ=0 EndX=4.4 EndY=-14 EndZ=0
    g14: LineSegment StartX=4.4 StartY=-14 StartZ=0 EndX=2.6 EndY=-18 EndZ=0
    g15: LineSegment StartX=4.4 StartY=-18 StartZ=0 EndX=2.6 EndY=-14 EndZ=0
    g16: GeomPoint X=3.5 Y=-16 Z=0
  constraints (42):
    c: Coincident(g0,g1)
    c: Coincident(g1,g2)
    c: Coincident(g2,g3)
    c: Coincident(g3,g0)
    c: Horizontal(g0)
    c: Horizontal(g2)
    c: Vertical(g1)
    c: Vertical(g3)
    c: Coincident(g4,g-3)
    c: PointOnObject(g4,g-4)
    c: PointOnObject(g4,g-2)
    c: PointOnObject(g5,g-3)
    c: Coincident(g5,g-4)
    c: PointOnObject(g5,g-2)
    c: PointOnObject(g6,g5)
    c: PointOnObject(g6,g4)
    c: Coincident(g7,g0)
    c: Coincident(g7,g1)
    c: Coincident(g8,g2)
    c: Coincident(g8,g0)
    c: PointOnObject(g9,g8)
    c: PointOnObject(g9,g7)
    c: Coincident(g10,g11)
    c: Coincident(g11,g12)
    c: Coincident(g12,g13)
    c: Coincident(g13,g10)
    c: Horizontal(g10)
    c: Horizontal(g12)
    c: Vertical(g11)
    c: Vertical(g13)
    c: Coincident(g14,g10)
    c: Coincident(g14,g11)
    c: Coincident(g15,g12)
    c: Coincident(g15,g10)
    c: PointOnObject(g16,g15)
    c: PointOnObject(g16,g14)
    c: Equal(g13,g1)
    c: Equal(g0,g10)
    c: Symmetric(g0,g10,g-2)
    c: DistanceX(g0,g0) = 1.8
    c: Coincident(g9,g6)
    c: DistanceY(g3,g3) = 4
FEATURE [PartDesign::Pad] Pad017
  BaseFeature = -> Pad016
  Direction = (0,0,1)
  Length = 1
  Length2 = 10
  Profile = -> Sketch023
  ReferenceAxis = -> Sketch023 [N_Axis]
  Type = 0
FEATURE [Sketcher::SketchObject] Sketch024
  ExternalGeometry = -> [Pad017]
  FullyConstrained = false
  MapMode = 5
  Placement = pos=(0,0,1.5) rot=(0,0,1;0rad)
  Support = -> [Pad017]
  sketch-geometry (5):
    g0: LineSegment StartX=3.6527 StartY=-18 StartZ=0 EndX=3.6527 EndY=-19.9557 EndZ=0
    g1: LineSegment StartX=3.90145 StartY=-20.2045 StartZ=0 EndX=5.253 EndY=-20.2045 EndZ=0
    g2: LineSegment StartX=6.27944 StartY=-21.2309 StartZ=0 EndX=6.27944 EndY=-25.0298 EndZ=0
    g3: ArcOfCircle CenterX=3.90145 CenterY=-19.9557 CenterZ=0 NormalX=0 NormalY=0 NormalZ=1 AngleXU=0 Radius=0.248751 StartAngle=3.14159 EndAngle=4.71239
    g4: ArcOfCircle CenterX=5.253 CenterY=-21.2309 CenterZ=0 NormalX=0 NormalY=0 NormalZ=1 AngleXU=0 Radius=1.02644 StartAngle=0 EndAngle=1.5708
  constraints (8):
    c: PointOnObject(g0,g-3)
    c: Vertical(g0)
    c: Horizontal(g1)
    c: Vertical(g2)
    c: Tangent(g0,g3) = -1.5708
    c: Tangent(g1,g3) = -1.5708
    c: Tangent(g1,g4) = 1.5708
    c: Tangent(g2,g4) = 1.5708
FEATURE [PartDesign::Plane] DatumPlane002
  Length = 60
  MapMode = 6
  Placement = pos=(6.27944,-25.0298,1.5) rot=(1,0,0;1.5708rad)
  ResizeMode = 0
  Support = -> [Sketch024,Pad017]
  Width = 60
FEATURE [Sketcher::SketchObject] Sketch025
  FullyConstrained = true
  MapMode = 5
  Placement = pos=(6.27944,-25.0298,1.5) rot=(1,0,0;1.5708rad)
  Support = -> [DatumPlane002]
  sketch-geometry (1):
    g0: Circle CenterX=0 CenterY=0 CenterZ=0 NormalX=0 NormalY=0 NormalZ=1 AngleXU=0 Radius=0.25
  constraints (2):
    c: Coincident(g0,g-1)
    c: Diameter(g0) = 0.5
FEATURE [PartDesign::AdditivePipe] AdditivePipe002
  AuxilleryCurvelinear = true
  AuxillerySpineTangent = false
  BaseFeature = -> Pad017
  Binormal = (0,0,0)
  Mode = 0
  Profile = -> Sketch025
  Spine = -> Sketch024
  SpineTangent = false
  Transformation = 0
  Transition = 0
FEATURE [Sketcher::SketchObject] Sketch026
  ExternalGeometry = -> [AdditivePipe002]
  FullyConstrained = false
  MapMode = 5
  Placement = pos=(0,0,1.5) rot=(0,0,1;0rad)
  Support = -> [AdditivePipe002]
  sketch-geometry (5):
    g0: LineSegment StartX=3.07914 StartY=-18 StartZ=0 EndX=1.90544 EndY=-20.1586 EndZ=0
    g1: LineSegment StartX=2.28825 StartY=-21.0844 StartZ=0 EndX=2.98106 EndY=-21.2901 EndZ=0
    g2: LineSegment StartX=3.55483 StartY=-22.0589 StartZ=0 EndX=3.55483 EndY=-25.0439 EndZ=0
    g3: ArcOfCircle CenterX=2.47169 CenterY=-20.4665 CenterZ=0 NormalX=0 NormalY=0 NormalZ=1 AngleXU=0 Radius=0.64454 StartAngle=2.64358 EndAngle=4.4238
    g4: ArcOfCircle CenterX=2.75281 CenterY=-22.0589 CenterZ=0 NormalX=0 NormalY=0 NormalZ=1 AngleXU=0 Radius=0.802026 StartAngle=0 EndAngle=1.28221
  constraints (6):
    c: PointOnObject(g0,g-3)
    c: Vertical(g2)
    c: Tangent(g0,g3) = -1.5708
    c: Tangent(g1,g3) = -1.5708
    c: Tangent(g1,g4) = 1.5708
    c: Tangent(g2,g4) = 1.5708
FEATURE [PartDesign::Plane] DatumPlane003
  Length = 60
  MapMode = 6
  Placement = pos=(3.55483,-25.0439,1.5) rot=(1,0,0;1.5708rad)
  ResizeMode = 0
  Support = -> [Sketch026,AdditivePipe002]
  Width = 60
FEATURE [Sketcher::SketchObject] Sketch027
  FullyConstrained = true
  MapMode = 5
  Placement = pos=(3.55483,-25.0439,1.5) rot=(1,0,0;1.5708rad)
  Support = -> [DatumPlane003]
  sketch-geometry (1):
    g0: Circle CenterX=0 CenterY=0 CenterZ=0 NormalX=0 NormalY=0 NormalZ=1 AngleXU=0 Radius=0.25
  constraints (2):
    c: Coincident(g0,g-1)
    c: Diameter(g0) = 0.5
FEATURE [PartDesign::AdditivePipe] AdditivePipe003
  AuxilleryCurvelinear = true
  AuxillerySpineTangent = false
  BaseFeature = -> AdditivePipe002
  Binormal = (0,0,0)
  Mode = 0
  Profile = -> Sketch027
  Spine = -> Sketch026
  SpineTangent = false
  Transformation = 0
  Transition = 0
FEATURE [PartDesign::Body] Body006  label="Battery001"
  Group = -> [Sketch021,Pad015,Sketch022,Pad016,Sketch023,Pad017,Sketch024,DatumPlane002,Sketch025,AdditivePipe002,Sketch026,DatumPlane003,Sketch027,AdditivePipe003]
  Origin = -> Origin010
  Placement = pos=(-30.7,3.7,19.9) rot=(0,1,0;3.14159rad)
  Tip = -> AdditivePipe003
FEATURE [App::Part] Part  label="Decoration"
  Group = -> [switch_mx009,switch_mx008,switch_mx007,switch_mx006,switch_mx005,switch_mx004,switch_mx003,switch_mx002,switch_mx001,switch_mx,Seeed_Studio_XIAO_RP2040_v26,Body002,Body003,Body004,Body006]
  Origin = -> Origin006
  Placement = pos=(0,0,0) rot=(0,1,0;3.14159rad)
FEATURE [Sketcher::SketchObject] Sketch
  FullyConstrained = true
  MapMode = 5
  Placement = pos=(0,0,0) rot=(1,0,0;3.14159rad)
  Support = -> [Pad014]
  expr: Constraints[10] = <<Spreadsheet>>.xiao_width - <<Spreadsheet>>.walls * 2
  expr: Constraints[8] = <<Spreadsheet>>.walls
  expr: Constraints[9] = 10mm + 1.5 * <<Spreadsheet>>.walls
  sketch-geometry (4):
    g0: LineSegment StartX=-7 StartY=-13 StartZ=0 EndX=7 EndY=-13 EndZ=0
    g1: LineSegment StartX=7 StartY=-13 StartZ=0 EndX=7 EndY=-15 EndZ=0
    g2: LineSegment StartX=7 StartY=-15 StartZ=0 EndX=-7 EndY=-15 EndZ=0
    g3: LineSegment StartX=-7 StartY=-15 StartZ=0 EndX=-7 EndY=-13 EndZ=0
  constraints (11):
    c: Coincident(g0,g1)
    c: Coincident(g1,g2)
    c: Coincident(g2,g3)
    c: Coincident(g3,g0)
    c: Horizontal(g2)
    c: Vertical(g1)
    c: Vertical(g3)
    c: Symmetric(g0,g0,g-2)
    c: DistanceY(g1,g1) = 2
    c: DistanceY(g0,g-1) = 13
    c: DistanceX(g2,g2) = 14
FEATURE [PartDesign::Pad] Pad
  BaseFeature = -> Pad014
  Direction = (0,0,-1)
  Length = 1.9
  Length2 = 10
  Profile = -> Sketch
  ReferenceAxis = -> Sketch [N_Axis]
  Type = 0
FEATURE [Sketcher::SketchObject] Sketch028
  FullyConstrained = false
  MapMode = 5
  Placement = pos=(0,0,0) rot=(1,0,0;3.14159rad)
  Support = -> [Pad]
  expr: Constraints[112] = <<Spreadsheet>>.keysize
  expr: Constraints[113] = <<Spreadsheet>>.keysize
  expr: Constraints[114] = <<Spreadsheet>>.spacing
  expr: Constraints[115] = <<Spreadsheet>>.keysize
  expr: Constraints[116] = <<Spreadsheet>>.keysize / 2
  expr: Constraints[13] = <<Spreadsheet>>.snapwidth
  expr: Constraints[14] = <<Spreadsheet>>.snaplength
  expr: Constraints[15] = <<Spreadsheet>>.keysize / 2
  expr: Constraints[33] = <<Spreadsheet>>.spacing
  expr: Constraints[4] = <<Spreadsheet>>.col3
  expr: Constraints[54] = <<Spreadsheet>>.keysize
  expr: Constraints[55] = <<Spreadsheet>>.col4
  expr: Constraints[60] = <<Spreadsheet>>.keysize
  expr: Constraints[61] = <<Spreadsheet>>.keysize / 2
  sketch-geometry (43):
    g0: LineSegment StartX=-14.55 StartY=29.1938 StartZ=0 EndX=-14.55 EndY=-29.0368 EndZ=0
    g1: LineSegment StartX=0 StartY=0 StartZ=0 EndX=-14.55 EndY=0 EndZ=0
    g2: LineSegment StartX=-17.05 StartY=7.85 StartZ=0 EndX=-12.05 EndY=7.85 EndZ=0
    g3: LineSegment StartX=-12.05 StartY=7.85 StartZ=0 EndX=-12.05 EndY=7.05 EndZ=0
    g4: LineSegment StartX=-12.05 StartY=7.05 StartZ=0 EndX=-17.05 EndY=7.05 EndZ=0
    g5: LineSegment StartX=-17.05 StartY=7.05 StartZ=0 EndX=-17.05 EndY=7.85 EndZ=0
    g6: LineSegment StartX=-17.05 StartY=9.05 StartZ=0 EndX=-12.05 EndY=9.05 EndZ=0
    g7: LineSegment StartX=-12.05 StartY=9.05 StartZ=0 EndX=-12.05 EndY=8.25 EndZ=0
    g8: LineSegment StartX=-12.05 StartY=8.25 StartZ=0 EndX=-17.05 EndY=8.25 EndZ=0
    g9: LineSegment StartX=-17.05 StartY=8.25 StartZ=0 EndX=-17.05 EndY=9.05 EndZ=0
    g10: LineSegment StartX=-17.05 StartY=23.95 StartZ=0 EndX=-12.05 EndY=23.95 EndZ=0
    g11: LineSegment StartX=-12.05 StartY=23.95 StartZ=0 EndX=-12.05 EndY=23.15 EndZ=0
    g12: LineSegment StartX=-12.05 StartY=23.15 StartZ=0 EndX=-17.05 EndY=23.15 EndZ=0
    g13: LineSegment StartX=-17.05 StartY=23.15 StartZ=0 EndX=-17.05 EndY=23.95 EndZ=0
    g14: LineSegment StartX=-33.15 StartY=31 StartZ=0 EndX=-28.15 EndY=31 EndZ=0
    g15: LineSegment StartX=-28.15 StartY=31 StartZ=0 EndX=-28.15 EndY=30.2 EndZ=0
    g16: LineSegment StartX=-28.15 StartY=30.2 StartZ=0 EndX=-33.15 EndY=30.2 EndZ=0
    g17: LineSegment StartX=-33.15 StartY=30.2 StartZ=0 EndX=-33.15 EndY=31 EndZ=0
    g18: LineSegment StartX=-33.15 StartY=16.1 StartZ=0 EndX=-28.15 EndY=16.1 EndZ=0
    g19: LineSegment StartX=-28.15 StartY=16.1 StartZ=0 EndX=-28.15 EndY=15.3 EndZ=0
    g20: LineSegment StartX=-28.15 StartY=15.3 StartZ=0 EndX=-33.15 EndY=15.3 EndZ=0
    g21: LineSegment StartX=-33.15 StartY=15.3 StartZ=0 EndX=-33.15 EndY=16.1 EndZ=0
    g22: LineSegment StartX=-30.65 StartY=35.578 StartZ=0 EndX=-30.65 EndY=-42.8131 EndZ=0
    g23: LineSegment StartX=-17.05 StartY=-7.85 StartZ=0 EndX=-12.05 EndY=-7.85 EndZ=0
    g24: LineSegment StartX=-12.05 StartY=-7.85 StartZ=0 EndX=-12.05 EndY=-7.05 EndZ=0
    g25: LineSegment StartX=-12.05 StartY=-7.05 StartZ=0 EndX=-17.05 EndY=-7.05 EndZ=0
    g26: LineSegment StartX=-17.05 StartY=-7.05 StartZ=0 EndX=-17.05 EndY=-7.85 EndZ=0
    g27: LineSegment StartX=-17.05 StartY=-9.05 StartZ=0 EndX=-12.05 EndY=-9.05 EndZ=0
    g28: LineSegment StartX=-12.05 StartY=-9.05 StartZ=0 EndX=-12.05 EndY=-8.25 EndZ=0
    g29: LineSegment StartX=-12.05 StartY=-8.25 StartZ=0 EndX=-17.05 EndY=-8.25 EndZ=0
    g30: LineSegment StartX=-17.05 StartY=-8.25 StartZ=0 EndX=-17.05 EndY=-9.05 EndZ=0
    g31: LineSegment StartX=-17.05 StartY=-23.95 StartZ=0 EndX=-12.05 EndY=-23.95 EndZ=0
    g32: LineSegment StartX=-12.05 StartY=-23.95 StartZ=0 EndX=-12.05 EndY=-23.15 EndZ=0
    g33: LineSegment StartX=-12.05 StartY=-23.15 StartZ=0 EndX=-17.05 EndY=-23.15 EndZ=0
    g34: LineSegment StartX=-17.05 StartY=-23.15 StartZ=0 EndX=-17.05 EndY=-23.95 EndZ=0
    g35: LineSegment StartX=-33.15 StartY=-31 StartZ=0 EndX=-28.15 EndY=-31 EndZ=0
    g36: LineSegment StartX=-28.15 StartY=-31 StartZ=0 EndX=-28.15 EndY=-30.2 EndZ=0
    g37: LineSegment StartX=-28.15 StartY=-30.2 StartZ=0 EndX=-33.15 EndY=-30.2 EndZ=0
    g38: LineSegment StartX=-33.15 StartY=-30.2 StartZ=0 EndX=-33.15 EndY=-31 EndZ=0
    g39: LineSegment StartX=-33.15 StartY=-16.1 StartZ=0 EndX=-28.15 EndY=-16.1 EndZ=0
    g40: LineSegment StartX=-28.15 StartY=-16.1 StartZ=0 EndX=-28.15 EndY=-15.3 EndZ=0
    g41: LineSegment StartX=-28.15 StartY=-15.3 StartZ=0 EndX=-33.15 EndY=-15.3 EndZ=0
    g42: LineSegment StartX=-33.15 StartY=-15.3 StartZ=0 EndX=-33.15 EndY=-16.1 EndZ=0
  constraints (117):
    c: Vertical(g0)
    c: Coincident(g1,g-1)
    c: PointOnObject(g1,g0)
    c: Horizontal(g1)
    c: DistanceX(g1,g1) = 14.55
    c: Coincident(g2,g3)
    c: Coincident(g3,g4)
    c: Coincident(g4,g5)
    c: Coincident(g5,g2)
    c: Horizontal(g4)
    c: Vertical(g3)
    c: Vertical(g5)
    c: Symmetric(g2,g2,g0)
    c: DistanceX(g2,g2) = 5
    c: DistanceY(g5,g5) = 0.8
    c: DistanceY(g1,g4) = 7.05
    c: Coincident(g6,g7)
    c: Coincident(g7,g8)
    c: Coincident(g8,g9)
    c: Coincident(g9,g6)
    c: Horizontal(g8)
    c: Vertical(g7)
    c: Vertical(g9)
    c: Equal(g2,g6) = 5
    c: Equal(g5,g9) = 1
    c: Symmetric(g6,g6,g0)
    c: Coincident(g10,g11)
    c: Coincident(g11,g12)
    c: Coincident(g12,g13)
    c: Coincident(g13,g10)
    c: Horizontal(g12)
    c: Vertical(g11)
    c: Vertical(g13)
    c: DistanceY(g4,g6) = 2
    c: Equal(g13,g9)
    c: Equal(g10,g6)
    c: Coincident(g14,g15)
    c: Coincident(g15,g16)
    c: Coincident(g16,g17)
    c: Coincident(g17,g14)
    c: Horizontal(g16)
    c: Vertical(g15)
    c: Vertical(g17)
    c: Horizontal(g14)
    c: Coincident(g18,g19)
    c: Coincident(g19,g20)
    c: Coincident(g20,g21)
    c: Coincident(g21,g18)
    c: Horizontal(g20)
    c: Vertical(g19)
    c: Vertical(g21)
    c: Equal(g14,g10)
    c: Equal(g15,g11)
    c: Symmetric(g10,g10,g0)
    c: DistanceY(g6,g12) = 14.1
    c: DistanceX(g22,g1) = 30.65
    c: Symmetric(g14,g14,g22)
    c: Equal(g14,g18)
    c: Equal(g15,g19)
    c: Symmetric(g18,g18,g22)
    c: DistanceY(g18,g16) = 14.1
    c: DistanceY(g12,g15) = 7.05
    c: Coincident(g23,g24)
    c: Coincident(g24,g25)
    c: Coincident(g25,g26)
    c: Coincident(g26,g23)
    c: Vertical(g24)
    c: Vertical(g26)
    c: Coincident(g27,g28)
    c: Coincident(g28,g29)
    c: Coincident(g29,g30)
    c: Coincident(g30,g27)
    c: Vertical(g28)
    c: Vertical(g30)
    c: Equal(g23,g27) = 5
    c: Equal(g26,g30) = 1
    c: Coincident(g31,g32)
    c: Coincident(g32,g33)
    c: Coincident(g33,g34)
    c: Coincident(g34,g31)
    c: Vertical(g32)
    c: Vertical(g34)
    c: Equal(g34,g30)
    c: Equal(g31,g27)
    c: Coincident(g35,g36)
    c: Coincident(g36,g37)
    c: Coincident(g37,g38)
    c: Coincident(g38,g35)
    c: Vertical(g36)
    c: Vertical(g38)
    c: Horizontal(g35)
    c: Coincident(g39,g40)
    c: Coincident(g40,g41)
    c: Coincident(g41,g42)
    c: Coincident(g42,g39)
    c: Horizontal(g41)
    c: Vertical(g40)
    c: Vertical(g42)
    c: Equal(g35,g31)
    c: Equal(g36,g32)
    c: Equal(g35,g39)
    c: Equal(g36,g40)
    c: Horizontal(g23)
    c: Horizontal(g27)
    c: Horizontal(g31)
    c: Equal(g26,g5)
    c: Equal(g25,g4)
    c: Symmetric(g25,g24,g0)
    c: Symmetric(g29,g28,g0)
    c: Symmetric(g33,g32,g0)
    c: Symmetric(g39,g39,g22)
    c: Symmetric(g37,g36,g22)
    c: DistanceY(g37,g39) = 14.1
    c: DistanceY(g33,g27) = 14.1
    c: DistanceY(g27,g25) = 2
    c: DistanceY(g25,g4) = 14.1
    c: DistanceY(g33,g39) = 7.05
FEATURE [PartDesign::Pocket] Pocket004
  BaseFeature = -> Pad
  Direction = (0,0,1)
  Length = 0.5
  Length2 = 5
  Profile = -> Sketch028
  ReferenceAxis = -> Sketch028 [N_Axis]
  Type = 0
  expr: Length = <<Spreadsheet>>.walls - 1.5mm
FEATURE [PartDesign::Mirrored] Mirrored
  BaseFeature = -> Pocket004
  MirrorPlane = -> Sketch028 [V_Axis]
  Originals = -> [Pocket004]
FEATURE [PartDesign::Body] Body005  label="switchplate"
  Group = -> [Sketch020,Pad014,Sketch,Pad,Sketch028,Pocket004,Mirrored]
  Origin = -> Origin009
  Placement = pos=(0,0,-13.7) rot=(0,0,1;0rad)
  Tip = -> Mirrored
